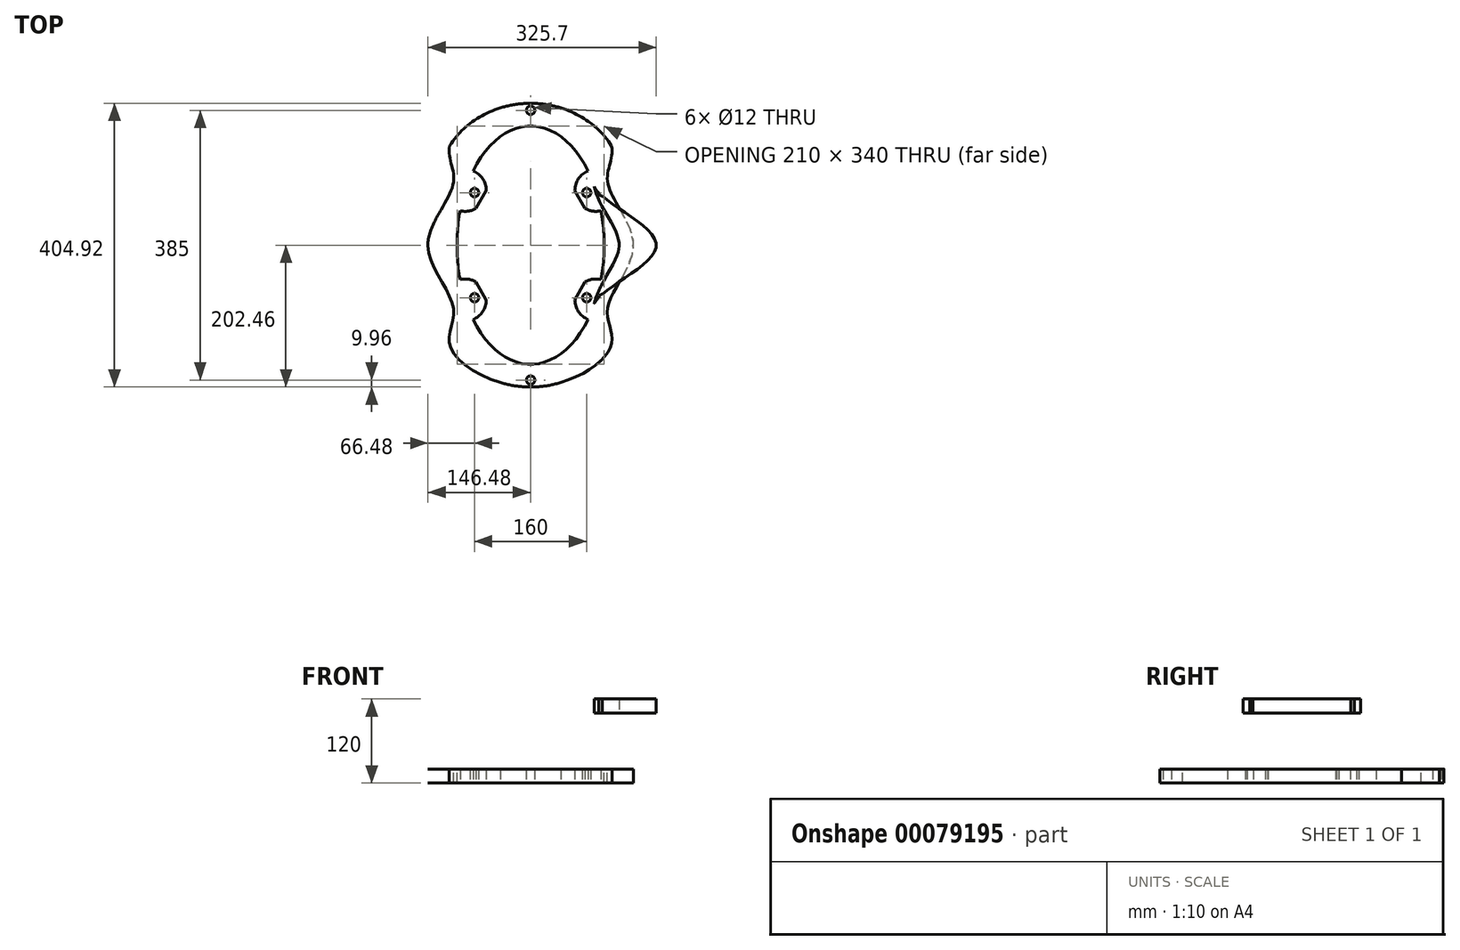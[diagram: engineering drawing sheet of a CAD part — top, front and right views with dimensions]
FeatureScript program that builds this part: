
annotation { "Feature Type Name" : "Feature", "Feature Type Description" : "" }
export const myFeature = defineFeature(function(context is Context, id is Id, definition is map)
    precondition{}
    {
        {
            var Q0;
            Q0=qCreatedBy(makeId("Top.planeOp"),FACE);
            var sketch = newSketch(context, id + "F0", { "sketchPlane" : qUnion([Q0])});
            skPoint(sketch, "E0", {"position": v(150.32, -165.76) * mm});
            skPoint(sketch, "E1", {"position": v(107.37, -221.56) * mm});
            skPoint(sketch, "E2", {"position": v(69.02, -211.72) * mm});
            skPoint(sketch, "E3", {"position": v(0, -246.18) * mm});
            skPoint(sketch, "E4", {"position": v(138.05, -177.25) * mm});
            skPoint(sketch, "E5", {"position": v(146.48, 0) * mm});
            skPoint(sketch, "E6", {"position": v(132.68, -82.88) * mm});
            skLineSegment(sketch, "E7", {"start": v(0, 292) * mm, "end": v(0, -246.18) * mm, "construction": true});
            skPoint(sketch, "E8.MirrorP", {"position": v(-146.48, 0) * mm});
            skPoint(sketch, "E9.MirrorP", {"position": v(-132.68, -82.88) * mm});
            skPoint(sketch, "E10.MirrorP", {"position": v(-150.32, -165.76) * mm});
            skPoint(sketch, "E11.MirrorP", {"position": v(-138.05, -177.25) * mm});
            skPoint(sketch, "E12.MirrorP", {"position": v(-107.37, -221.56) * mm});
            skPoint(sketch, "E13.MirrorP", {"position": v(-69.02, -211.72) * mm});
            skPoint(sketch, "E14", {"position": v(0, 0) * mm});
            skPoint(sketch, "E15", {"position": v(-146.25, -161.4) * mm});
            skPoint(sketch, "E16", {"position": v(-136.87, -189.28) * mm});
            skPoint(sketch, "E17", {"position": v(-146.26, -172.33) * mm});
            skPoint(sketch, "E18", {"position": v(-131.04, -210.06) * mm});
            skPoint(sketch, "E19", {"position": v(-94.82, -218.38) * mm});
            skPoint(sketch, "E20", {"position": v(-60.59, -222.84) * mm});
            skPoint(sketch, "E21", {"position": v(-67.25, -214.49) * mm});
            skPoint(sketch, "E22", {"position": v(-72.48, -210.2) * mm});
            skPoint(sketch, "E23", {"position": v(-119.37, -219.05) * mm});
            skPoint(sketch, "E24", {"position": v(-149.89, -167.68) * mm});
            skPoint(sketch, "E25.MirrorP", {"position": v(60.59, -222.84) * mm});
            skPoint(sketch, "E26.MirrorP", {"position": v(67.25, -214.49) * mm});
            skPoint(sketch, "E27.MirrorP", {"position": v(72.48, -210.2) * mm});
            skPoint(sketch, "E28.MirrorP", {"position": v(94.82, -218.38) * mm});
            skPoint(sketch, "E29.MirrorP", {"position": v(119.37, -219.05) * mm});
            skPoint(sketch, "E30.MirrorP", {"position": v(136.87, -189.28) * mm});
            skPoint(sketch, "E31.MirrorP", {"position": v(146.26, -172.33) * mm});
            skPoint(sketch, "E32.MirrorP", {"position": v(149.89, -167.68) * mm});
            skPoint(sketch, "E33.MirrorP", {"position": v(146.25, -161.4) * mm});
            skPoint(sketch, "E34", {"position": v(-139.73, -175.31) * mm});
            skPoint(sketch, "E35.MirrorP", {"position": v(131.04, -210.06) * mm});
            skPoint(sketch, "E36.MirrorP", {"position": v(-132.68, 82.88) * mm});
            skPoint(sketch, "E37.MirrorP", {"position": v(-139.73, 175.31) * mm});
            skPoint(sketch, "E38.MirrorP", {"position": v(-150.32, 165.76) * mm});
            skPoint(sketch, "E39.MirrorP", {"position": v(69.02, 211.72) * mm});
            skPoint(sketch, "E40.MirrorP", {"position": v(150.32, 165.76) * mm});
            skPoint(sketch, "E41.MirrorP", {"position": v(-67.25, 214.49) * mm});
            skPoint(sketch, "E42.MirrorP", {"position": v(131.04, 210.06) * mm});
            skPoint(sketch, "E43.MirrorP", {"position": v(60.59, 222.84) * mm});
            skPoint(sketch, "E44.MirrorP", {"position": v(119.37, 219.05) * mm});
            skPoint(sketch, "E45.MirrorP", {"position": v(136.87, 189.28) * mm});
            skPoint(sketch, "E46.MirrorP", {"position": v(-72.48, 210.2) * mm});
            skPoint(sketch, "E47.MirrorP", {"position": v(-138.05, 177.25) * mm});
            skPoint(sketch, "E48.MirrorP", {"position": v(-69.02, 211.72) * mm});
            skPoint(sketch, "E49.MirrorP", {"position": v(72.48, 210.2) * mm});
            skPoint(sketch, "E50.MirrorP", {"position": v(-146.25, 161.4) * mm});
            skPoint(sketch, "E51.MirrorP", {"position": v(-136.87, 189.28) * mm});
            skPoint(sketch, "E52.MirrorP", {"position": v(138.05, 177.25) * mm});
            skPoint(sketch, "E53.MirrorP", {"position": v(67.25, 214.49) * mm});
            skPoint(sketch, "E54.MirrorP", {"position": v(-149.89, 167.68) * mm});
            skPoint(sketch, "E55.MirrorP", {"position": v(149.89, 167.68) * mm});
            skPoint(sketch, "E56.MirrorP", {"position": v(-107.37, 221.56) * mm});
            skPoint(sketch, "E57.MirrorP", {"position": v(-94.82, 218.38) * mm});
            skPoint(sketch, "E58.MirrorP", {"position": v(146.26, 172.33) * mm});
            skPoint(sketch, "E59.MirrorP", {"position": v(107.37, 221.56) * mm});
            skPoint(sketch, "E60.MirrorP", {"position": v(-131.04, 210.06) * mm});
            skPoint(sketch, "E61.MirrorP", {"position": v(94.82, 218.38) * mm});
            skPoint(sketch, "E62.MirrorP", {"position": v(146.25, 161.4) * mm});
            skPoint(sketch, "E63.MirrorP", {"position": v(0, 246.18) * mm});
            skPoint(sketch, "E64.MirrorP", {"position": v(-146.26, 172.33) * mm});
            skPoint(sketch, "E65.MirrorP", {"position": v(-119.37, 219.05) * mm});
            skPoint(sketch, "E66.MirrorP", {"position": v(-60.59, 222.84) * mm});
            skPoint(sketch, "E67.MirrorP", {"position": v(132.68, 82.88) * mm});
            skFitSpline(sketch, "E68", {"points": [v(-146.48, 0) * mm, v(-132.68, 82.88) * mm, v(-146.25, 161.4) * mm, v(-150.32, 165.76) * mm, v(-149.89, 167.68) * mm, v(-146.26, 172.33) * mm, v(-139.73, 175.31) * mm, v(-138.05, 177.25) * mm, v(-136.87, 189.28) * mm, v(-131.04, 210.06) * mm, v(-119.37, 219.05) * mm, v(-107.37, 221.56) * mm, v(-94.82, 218.38) * mm, v(-72.48, 210.2) * mm, v(-69.02, 211.72) * mm, v(-67.25, 214.49) * mm, v(-60.59, 222.84) * mm, v(0, 246.18) * mm, v(60.59, 222.84) * mm, v(67.25, 214.49) * mm, v(69.02, 211.72) * mm, v(72.48, 210.2) * mm, v(94.82, 218.38) * mm, v(107.37, 221.56) * mm, v(119.37, 219.05) * mm, v(131.04, 210.06) * mm, v(136.87, 189.28) * mm, v(138.05, 177.25) * mm, v(146.26, 172.33) * mm, v(149.89, 167.68) * mm, v(150.32, 165.76) * mm, v(146.25, 161.4) * mm, v(132.68, 82.88) * mm, v(146.48, 0) * mm, v(132.68, -82.88) * mm, v(146.25, -161.4) * mm, v(150.32, -165.76) * mm, v(149.89, -167.68) * mm, v(146.26, -172.33) * mm, v(138.05, -177.25) * mm, v(136.87, -189.28) * mm, v(131.04, -210.06) * mm, v(119.37, -219.05) * mm, v(107.37, -221.56) * mm, v(94.82, -218.38) * mm, v(72.48, -210.2) * mm, v(69.02, -211.72) * mm, v(67.25, -214.49) * mm, v(60.59, -222.84) * mm, v(0, -246.18) * mm, v(-60.59, -222.84) * mm, v(-67.25, -214.49) * mm, v(-69.02, -211.72) * mm, v(-72.48, -210.2) * mm, v(-94.82, -218.38) * mm, v(-107.37, -221.56) * mm, v(-119.37, -219.05) * mm, v(-131.04, -210.06) * mm, v(-136.87, -189.28) * mm, v(-138.05, -177.25) * mm, v(-139.73, -175.31) * mm, v(-146.26, -172.33) * mm, v(-149.89, -167.68) * mm, v(-150.32, -165.76) * mm, v(-146.25, -161.4) * mm, v(-132.68, -82.88) * mm, v(-146.48, 0) * mm]});
            skPoint(sketch, "E69", {"position": v(0, 295) * mm});
            skPoint(sketch, "E70", {"position": v(-30, 295) * mm});
            skPoint(sketch, "E71", {"position": v(-225, 0) * mm});
            skPoint(sketch, "E72", {"position": v(-225, 100) * mm});
            skPoint(sketch, "E73.MirrorP", {"position": v(225, 100) * mm});
            skPoint(sketch, "E74.MirrorP", {"position": v(225, -60) * mm});
            skLineSegment(sketch, "E75", {"start": v(0, 0) * mm, "end": v(-373.3, 215.53) * mm, "construction": true});
            skLineSegment(sketch, "E76", {"start": v(0, 0) * mm, "end": v(-204.64, 354.44) * mm, "construction": true});
            skLineSegment(sketch, "E77", {"start": v(-225, 0) * mm, "end": v(-225, 100) * mm});
            skLineSegment(sketch, "E78", {"start": v(-30, 295) * mm, "end": v(0, 295) * mm});
            skPoint(sketch, "E79", {"position": v(-30, 100) * mm});
            skArc(sketch, "E80", {"start": v(-30, 295) * mm, "mid": v(-167.89, 237.89) * mm, "end": v(-225, 100) * mm});
            skLineSegment(sketch, "E81.MirrorCS", {"start": v(225, 0) * mm, "end": v(225, 100) * mm});
            skArc(sketch, "E82.MirrorCS", {"start": v(30, 295) * mm, "mid": v(167.89, 237.89) * mm, "end": v(225, 100) * mm});
            skLineSegment(sketch, "E83.MirrorCS", {"start": v(30, 295) * mm, "end": v(0, 295) * mm});
            skArc(sketch, "E84.MirrorCS", {"start": v(-30, -295) * mm, "mid": v(-167.89, -237.89) * mm, "end": v(-225, -100) * mm});
            skLineSegment(sketch, "E85.MirrorCS", {"start": v(-225, 0) * mm, "end": v(-225, -100) * mm});
            skLineSegment(sketch, "E86.MirrorCS", {"start": v(225, 0) * mm, "end": v(225, -100) * mm});
            skArc(sketch, "E87.MirrorCS", {"start": v(30, -295) * mm, "mid": v(167.89, -237.89) * mm, "end": v(225, -100) * mm});
            skLineSegment(sketch, "E88.MirrorCS", {"start": v(30, -295) * mm, "end": v(0, -295) * mm});
            skLineSegment(sketch, "E89.MirrorCS", {"start": v(-30, -295) * mm, "end": v(0, -295) * mm});
            skEllipse(sketch, "E90", {"center": v(0, 82.88) * mm, "majorRadius": 132.68 * mm, "minorRadius": 119.58 * mm, "majorAxis": v(1, 0)});
            skSolve(sketch);
        }
        {
            var Q0;
            {var subQ0=sQuery(id+"F0.wireOp",EDGE,"E90");var subQ1=sQuery(id+"F0.wireOp",EDGE,"E68");var subQ2=makeQuery(id+"F0.imprint","INTERSECT",VERTEX,{"disambiguationData":[OD(1.0)],"derivedFrom":[subQ1,subQ0]});Q0=makeQuery(id+"F0.imprint","IMPRINT",FACE,{"disambiguationData":[TD([[makeQuery(id+"F0.imprint","IMPRINT",EDGE,{"disambiguationData":[TD([[subQ2,1.0]])],"derivedFrom":subQ1}),-1.0]])]});}
            cPlane(context, id + "F1", {"entities" : qUnion([Q0]), "cplaneType" : CPlaneType.OFFSET, "offset" : 100 * mm, "width" : 150 * mm, "height" : 150 * mm});
        }
        {
            var Q0;
            {var subQ0=sQuery(id+"F0.wireOp",EDGE,"E90");var subQ1=sQuery(id+"F0.wireOp",EDGE,"E68");var subQ2=makeQuery(id+"F0.imprint","INTERSECT",VERTEX,{"disambiguationData":[OD(0.0)],"derivedFrom":[subQ1,subQ0]});Q0=makeQuery(id+"F0.imprint","IMPRINT",FACE,{"disambiguationData":[TD([[makeQuery(id+"F0.imprint","IMPRINT",EDGE,{"disambiguationData":[TD([[subQ2,1.0]])],"derivedFrom":subQ1}),-1.0]])]});}
            var sketch = newSketch(context, id + "F2", { "sketchPlane" : qUnion([Q0])});
            skFitSpline(sketch, "E91.0", {"points": [v(-146.48, 0) * mm, v(-146.48, 25.45) * mm, v(-122.55, 75.68) * mm, v(-141.58, 161.6) * mm, v(-150.97, 165.24) * mm, v(-149.84, 167.93) * mm, v(-146.88, 173.13) * mm, v(-139.54, 174.98) * mm, v(-137.39, 177.3) * mm, v(-137.38, 190.15) * mm, v(-133.28, 211.38) * mm, v(-119.9, 219.69) * mm, v(-106.83, 222.51) * mm, v(-95.46, 219.19) * mm, v(-72.9, 208.32) * mm, v(-68.89, 211.56) * mm, v(-66.98, 214.97) * mm, v(-60.9, 225.94) * mm, v(0, 260.58) * mm, v(60.9, 225.94) * mm, v(66.98, 214.97) * mm, v(68.89, 211.56) * mm, v(72.9, 208.32) * mm, v(95.47, 219.19) * mm, v(106.82, 222.52) * mm, v(119.95, 219.67) * mm, v(133.09, 211.44) * mm, v(138.2, 189.9) * mm, v(135.3, 175.97) * mm, v(146.9, 173.38) * mm, v(149.81, 167.94) * mm, v(150.98, 165.24) * mm, v(141.57, 161.6) * mm, v(122.55, 75.68) * mm, v(158.6, 0) * mm, v(122.55, -75.68) * mm, v(141.57, -161.6) * mm, v(150.98, -165.24) * mm, v(149.81, -167.94) * mm, v(146.9, -173.38) * mm, v(135.3, -175.97) * mm, v(138.2, -189.9) * mm, v(133.09, -211.44) * mm, v(119.95, -219.67) * mm, v(106.82, -222.52) * mm, v(95.47, -219.19) * mm, v(72.9, -208.32) * mm, v(68.89, -211.56) * mm, v(66.98, -214.97) * mm, v(60.9, -225.94) * mm, v(0, -260.58) * mm, v(-60.9, -225.94) * mm, v(-66.98, -214.97) * mm, v(-68.89, -211.56) * mm, v(-72.9, -208.32) * mm, v(-95.46, -219.19) * mm, v(-106.83, -222.51) * mm, v(-119.9, -219.69) * mm, v(-133.28, -211.38) * mm, v(-137.38, -190.15) * mm, v(-137.39, -177.3) * mm, v(-139.54, -174.98) * mm, v(-146.88, -173.13) * mm, v(-149.84, -167.93) * mm, v(-150.97, -165.24) * mm, v(-141.58, -161.6) * mm, v(-122.55, -75.68) * mm, v(-146.48, -25.45) * mm, v(-146.48, 0) * mm]});
            skEllipticalArc(sketch, "E92.0", {});
            skEllipticalArc(sketch, "E93.MirrorC", {});
            skFitSpline(sketch, "E94.trimOffspring", {"points": [v(-146.48, 0) * mm, v(-146.48, 25.45) * mm, v(-122.55, 75.68) * mm, v(-141.58, 161.6) * mm, v(-150.97, 165.24) * mm, v(-149.84, 167.93) * mm, v(-146.88, 173.13) * mm, v(-139.54, 174.98) * mm, v(-137.39, 177.3) * mm, v(-137.38, 190.15) * mm, v(-133.28, 211.38) * mm, v(-119.9, 219.69) * mm, v(-106.83, 222.51) * mm, v(-95.46, 219.19) * mm, v(-72.9, 208.32) * mm, v(-68.89, 211.56) * mm, v(-66.98, 214.97) * mm, v(-60.9, 225.94) * mm, v(0, 260.58) * mm, v(60.9, 225.94) * mm, v(66.98, 214.97) * mm, v(68.89, 211.56) * mm, v(72.9, 208.32) * mm, v(95.47, 219.19) * mm, v(106.82, 222.52) * mm, v(119.95, 219.67) * mm, v(133.09, 211.44) * mm, v(138.2, 189.9) * mm, v(135.3, 175.97) * mm, v(146.9, 173.38) * mm, v(149.81, 167.94) * mm, v(150.98, 165.24) * mm, v(141.57, 161.6) * mm, v(122.55, 75.68) * mm, v(158.6, 0) * mm, v(122.55, -75.68) * mm, v(141.57, -161.6) * mm, v(150.98, -165.24) * mm, v(149.81, -167.94) * mm, v(146.9, -173.38) * mm, v(135.3, -175.97) * mm, v(138.2, -189.9) * mm, v(133.09, -211.44) * mm, v(119.95, -219.67) * mm, v(106.82, -222.52) * mm, v(95.47, -219.19) * mm, v(72.9, -208.32) * mm, v(68.89, -211.56) * mm, v(66.98, -214.97) * mm, v(60.9, -225.94) * mm, v(0, -260.58) * mm, v(-60.9, -225.94) * mm, v(-66.98, -214.97) * mm, v(-68.89, -211.56) * mm, v(-72.9, -208.32) * mm, v(-95.46, -219.19) * mm, v(-106.83, -222.51) * mm, v(-119.9, -219.69) * mm, v(-133.28, -211.38) * mm, v(-137.38, -190.15) * mm, v(-137.39, -177.3) * mm, v(-139.54, -174.98) * mm, v(-146.88, -173.13) * mm, v(-149.84, -167.93) * mm, v(-150.97, -165.24) * mm, v(-141.58, -161.6) * mm, v(-122.55, -75.68) * mm, v(-146.48, -25.45) * mm, v(-146.48, 0) * mm]});
            skPoint(sketch, "E95", {"position": v(0, 202.46) * mm});
            skPoint(sketch, "E96", {"position": v(-110, 90) * mm});
            skPoint(sketch, "E97", {"position": v(-115, 143) * mm});
            skPoint(sketch, "E98.MirrorP", {"position": v(115, 143) * mm});
            skPoint(sketch, "E99.MirrorP", {"position": v(110, 90) * mm});
            skPoint(sketch, "E100.MirrorP", {"position": v(-110, -90) * mm});
            skPoint(sketch, "E101.MirrorP", {"position": v(-115, -143) * mm});
            skPoint(sketch, "E102.MirrorP", {"position": v(0, -202.46) * mm});
            skPoint(sketch, "E103.MirrorP", {"position": v(115, -143) * mm});
            skPoint(sketch, "E104.MirrorP", {"position": v(110, -90) * mm});
            skFitSpline(sketch, "E105", {"points": [v(-146.48, 0) * mm, v(-110, 90) * mm, v(-115, 143) * mm, v(0, 202.46) * mm, v(115, 143) * mm, v(110, 90) * mm, v(146.48, 0) * mm, v(110, -90) * mm, v(115, -143) * mm, v(0, -202.46) * mm, v(-115, -143) * mm, v(-110, -90) * mm, v(-146.48, 0) * mm]});
            skFitSpline(sketch, "E106.trimOffspring", {"points": [v(-146.48, 0) * mm, v(-146.48, 25.45) * mm, v(-122.55, 75.68) * mm, v(-141.58, 161.6) * mm, v(-150.97, 165.24) * mm, v(-149.84, 167.93) * mm, v(-146.88, 173.13) * mm, v(-139.54, 174.98) * mm, v(-137.39, 177.3) * mm, v(-137.38, 190.15) * mm, v(-133.28, 211.38) * mm, v(-119.9, 219.69) * mm, v(-106.83, 222.51) * mm, v(-95.46, 219.19) * mm, v(-72.9, 208.32) * mm, v(-68.89, 211.56) * mm, v(-66.98, 214.97) * mm, v(-60.9, 225.94) * mm, v(0, 260.58) * mm, v(60.9, 225.94) * mm, v(66.98, 214.97) * mm, v(68.89, 211.56) * mm, v(72.9, 208.32) * mm, v(95.47, 219.19) * mm, v(106.82, 222.52) * mm, v(119.95, 219.67) * mm, v(133.09, 211.44) * mm, v(138.2, 189.9) * mm, v(135.3, 175.97) * mm, v(146.9, 173.38) * mm, v(149.81, 167.94) * mm, v(150.98, 165.24) * mm, v(141.57, 161.6) * mm, v(122.55, 75.68) * mm, v(158.6, 0) * mm, v(122.55, -75.68) * mm, v(141.57, -161.6) * mm, v(150.98, -165.24) * mm, v(149.81, -167.94) * mm, v(146.9, -173.38) * mm, v(135.3, -175.97) * mm, v(138.2, -189.9) * mm, v(133.09, -211.44) * mm, v(119.95, -219.67) * mm, v(106.82, -222.52) * mm, v(95.47, -219.19) * mm, v(72.9, -208.32) * mm, v(68.89, -211.56) * mm, v(66.98, -214.97) * mm, v(60.9, -225.94) * mm, v(0, -260.58) * mm, v(-60.9, -225.94) * mm, v(-66.98, -214.97) * mm, v(-68.89, -211.56) * mm, v(-72.9, -208.32) * mm, v(-95.46, -219.19) * mm, v(-106.83, -222.51) * mm, v(-119.9, -219.69) * mm, v(-133.28, -211.38) * mm, v(-137.38, -190.15) * mm, v(-137.39, -177.3) * mm, v(-139.54, -174.98) * mm, v(-146.88, -173.13) * mm, v(-149.84, -167.93) * mm, v(-150.97, -165.24) * mm, v(-141.58, -161.6) * mm, v(-122.55, -75.68) * mm, v(-146.48, -25.45) * mm, v(-146.48, 0) * mm]});
            skFitSpline(sketch, "E107.trimOffspring", {"points": [v(-146.48, 0) * mm, v(-146.48, 25.45) * mm, v(-122.55, 75.68) * mm, v(-141.58, 161.6) * mm, v(-150.97, 165.24) * mm, v(-149.84, 167.93) * mm, v(-146.88, 173.13) * mm, v(-139.54, 174.98) * mm, v(-137.39, 177.3) * mm, v(-137.38, 190.15) * mm, v(-133.28, 211.38) * mm, v(-119.9, 219.69) * mm, v(-106.83, 222.51) * mm, v(-95.46, 219.19) * mm, v(-72.9, 208.32) * mm, v(-68.89, 211.56) * mm, v(-66.98, 214.97) * mm, v(-60.9, 225.94) * mm, v(0, 260.58) * mm, v(60.9, 225.94) * mm, v(66.98, 214.97) * mm, v(68.89, 211.56) * mm, v(72.9, 208.32) * mm, v(95.47, 219.19) * mm, v(106.82, 222.52) * mm, v(119.95, 219.67) * mm, v(133.09, 211.44) * mm, v(138.2, 189.9) * mm, v(135.3, 175.97) * mm, v(146.9, 173.38) * mm, v(149.81, 167.94) * mm, v(150.98, 165.24) * mm, v(141.57, 161.6) * mm, v(122.55, 75.68) * mm, v(158.6, 0) * mm, v(122.55, -75.68) * mm, v(141.57, -161.6) * mm, v(150.98, -165.24) * mm, v(149.81, -167.94) * mm, v(146.9, -173.38) * mm, v(135.3, -175.97) * mm, v(138.2, -189.9) * mm, v(133.09, -211.44) * mm, v(119.95, -219.67) * mm, v(106.82, -222.52) * mm, v(95.47, -219.19) * mm, v(72.9, -208.32) * mm, v(68.89, -211.56) * mm, v(66.98, -214.97) * mm, v(60.9, -225.94) * mm, v(0, -260.58) * mm, v(-60.9, -225.94) * mm, v(-66.98, -214.97) * mm, v(-68.89, -211.56) * mm, v(-72.9, -208.32) * mm, v(-95.46, -219.19) * mm, v(-106.83, -222.51) * mm, v(-119.9, -219.69) * mm, v(-133.28, -211.38) * mm, v(-137.38, -190.15) * mm, v(-137.39, -177.3) * mm, v(-139.54, -174.98) * mm, v(-146.88, -173.13) * mm, v(-149.84, -167.93) * mm, v(-150.97, -165.24) * mm, v(-141.58, -161.6) * mm, v(-122.55, -75.68) * mm, v(-146.48, -25.45) * mm, v(-146.48, 0) * mm]});
            skFitSpline(sketch, "E108.trimOffspring", {"points": [v(-146.48, 0) * mm, v(-146.48, 25.45) * mm, v(-122.55, 75.68) * mm, v(-141.58, 161.6) * mm, v(-150.97, 165.24) * mm, v(-149.84, 167.93) * mm, v(-146.88, 173.13) * mm, v(-139.54, 174.98) * mm, v(-137.39, 177.3) * mm, v(-137.38, 190.15) * mm, v(-133.28, 211.38) * mm, v(-119.9, 219.69) * mm, v(-106.83, 222.51) * mm, v(-95.46, 219.19) * mm, v(-72.9, 208.32) * mm, v(-68.89, 211.56) * mm, v(-66.98, 214.97) * mm, v(-60.9, 225.94) * mm, v(0, 260.58) * mm, v(60.9, 225.94) * mm, v(66.98, 214.97) * mm, v(68.89, 211.56) * mm, v(72.9, 208.32) * mm, v(95.47, 219.19) * mm, v(106.82, 222.52) * mm, v(119.95, 219.67) * mm, v(133.09, 211.44) * mm, v(138.2, 189.9) * mm, v(135.3, 175.97) * mm, v(146.9, 173.38) * mm, v(149.81, 167.94) * mm, v(150.98, 165.24) * mm, v(141.57, 161.6) * mm, v(122.55, 75.68) * mm, v(158.6, 0) * mm, v(122.55, -75.68) * mm, v(141.57, -161.6) * mm, v(150.98, -165.24) * mm, v(149.81, -167.94) * mm, v(146.9, -173.38) * mm, v(135.3, -175.97) * mm, v(138.2, -189.9) * mm, v(133.09, -211.44) * mm, v(119.95, -219.67) * mm, v(106.82, -222.52) * mm, v(95.47, -219.19) * mm, v(72.9, -208.32) * mm, v(68.89, -211.56) * mm, v(66.98, -214.97) * mm, v(60.9, -225.94) * mm, v(0, -260.58) * mm, v(-60.9, -225.94) * mm, v(-66.98, -214.97) * mm, v(-68.89, -211.56) * mm, v(-72.9, -208.32) * mm, v(-95.46, -219.19) * mm, v(-106.83, -222.51) * mm, v(-119.9, -219.69) * mm, v(-133.28, -211.38) * mm, v(-137.38, -190.15) * mm, v(-137.39, -177.3) * mm, v(-139.54, -174.98) * mm, v(-146.88, -173.13) * mm, v(-149.84, -167.93) * mm, v(-150.97, -165.24) * mm, v(-141.58, -161.6) * mm, v(-122.55, -75.68) * mm, v(-146.48, -25.45) * mm, v(-146.48, 0) * mm]});
            skEllipticalArc(sketch, "E109.trimOffspring", {});
            skEllipticalArc(sketch, "E110.trimOffspring", {});
            skEllipticalArc(sketch, "E111.trimOffspring", {});
            skEllipticalArc(sketch, "E112.trimOffspring", {});
            skCircle(sketch, "E113", {"center": v(0, 192.5) * mm, "radius": 6 * mm});
            skLineSegment(sketch, "E114", {"start": v(-226.31, 0) * mm, "end": v(229.86, 0) * mm, "construction": true});
            skCircle(sketch, "E115.MirrorC", {"center": v(0, -192.5) * mm, "radius": 6 * mm});
            skPoint(sketch, "E116", {"position": v(-80, 75) * mm});
            skCircle(sketch, "E117", {"center": v(-80, 75) * mm, "radius": 6 * mm});
            skArc(sketch, "E118", {"start": v(-100.52, 49.11) * mm, "mid": v(-88.85, 48.53) * mm, "end": v(-77.84, 52.46) * mm});
            skFitSpline(sketch, "E119.0", {"points": [v(-126.48, -0.62) * mm, v(-126.48, 0) * mm, v(-126.48, 0.62) * mm, v(-126.45, 1.48) * mm, v(-126.37, 2.57) * mm, v(-126.23, 3.92) * mm, v(-125.95, 5.8) * mm, v(-125.44, 8.25) * mm, v(-124.57, 11.4) * mm, v(-123.44, 14.7) * mm, v(-121.62, 19.33) * mm, v(-118.77, 25.43) * mm, v(-114.67, 33.14) * mm, v(-110.1, 41.14) * mm, v(-105.34, 49.38) * mm, v(-101.43, 56.47) * mm, v(-98.47, 62.31) * mm, v(-96.37, 66.81) * mm, v(-94.44, 71.44) * mm, v(-93, 75.45) * mm, v(-92, 78.76) * mm, v(-91.33, 81.3) * mm, v(-90.75, 83.9) * mm, v(-90.35, 86.12) * mm, v(-90.1, 87.93) * mm, v(-89.88, 89.73) * mm, v(-89.7, 91.94) * mm, v(-89.6, 94.53) * mm, v(-89.61, 97.06) * mm, v(-89.72, 99.51) * mm, v(-89.98, 102.68) * mm, v(-90.47, 106.44) * mm, v(-91.26, 110.63) * mm, v(-92.14, 114.5) * mm, v(-93.04, 118.06) * mm, v(-94.2, 122.4) * mm, v(-95.17, 126.15) * mm, v(-95.82, 129.29) * mm, v(-96.14, 131.32) * mm, v(-96.3, 133.04) * mm, v(-96.31, 134.46) * mm, v(-96.23, 135.45) * mm, v(-96.11, 136.18) * mm, v(-96.02, 136.62) * mm, v(-95.93, 136.97) * mm, v(-95.85, 137.24) * mm, v(-95.76, 137.52) * mm, v(-95.62, 137.93) * mm, v(-95.4, 138.5) * mm, v(-94.93, 139.51) * mm, v(-94.14, 140.98) * mm, v(-92.83, 143) * mm, v(-91.14, 145.21) * mm, v(-89.1, 147.56) * mm, v(-86.7, 150.02) * mm, v(-83.04, 153.37) * mm, v(-77.67, 157.62) * mm, v(-70.12, 162.62) * mm, v(-61.63, 167.33) * mm, v(-52.35, 171.62) * mm, v(-42.46, 175.35) * mm, v(-32.12, 178.4) * mm, v(-23.26, 180.32) * mm, v(-16.1, 181.41) * mm, v(-10.72, 182.01) * mm, v(-6.24, 182.32) * mm, v(-2.67, 182.44) * mm, v(0, 182.47) * mm, v(2.67, 182.44) * mm, v(6.24, 182.32) * mm, v(10.72, 182.01) * mm, v(16.1, 181.41) * mm, v(23.26, 180.32) * mm, v(32.12, 178.4) * mm, v(42.46, 175.35) * mm, v(52.35, 171.62) * mm, v(61.63, 167.33) * mm, v(70.12, 162.62) * mm, v(77.67, 157.62) * mm, v(83.04, 153.37) * mm, v(86.7, 150.02) * mm, v(89.1, 147.56) * mm, v(91.14, 145.21) * mm, v(92.83, 143) * mm, v(94.14, 140.98) * mm, v(94.93, 139.51) * mm, v(95.4, 138.5) * mm, v(95.62, 137.93) * mm, v(95.76, 137.52) * mm, v(95.85, 137.24) * mm, v(95.93, 136.97) * mm, v(96.02, 136.62) * mm, v(96.11, 136.18) * mm, v(96.23, 135.45) * mm, v(96.31, 134.46) * mm, v(96.3, 133.04) * mm, v(96.14, 131.32) * mm, v(95.82, 129.29) * mm, v(95.17, 126.15) * mm, v(94.2, 122.4) * mm, v(93.04, 118.06) * mm, v(92.14, 114.5) * mm, v(91.26, 110.63) * mm, v(90.47, 106.44) * mm, v(89.98, 102.68) * mm, v(89.72, 99.51) * mm, v(89.61, 97.06) * mm, v(89.6, 94.53) * mm, v(89.7, 91.94) * mm, v(89.88, 89.73) * mm, v(90.1, 87.93) * mm, v(90.35, 86.12) * mm, v(90.75, 83.9) * mm, v(91.33, 81.3) * mm, v(92, 78.76) * mm, v(93, 75.45) * mm, v(94.44, 71.44) * mm, v(96.37, 66.81) * mm, v(98.47, 62.31) * mm, v(101.43, 56.47) * mm, v(105.34, 49.38) * mm, v(110.1, 41.14) * mm, v(114.67, 33.14) * mm, v(118.77, 25.43) * mm, v(121.62, 19.33) * mm, v(123.44, 14.7) * mm, v(124.57, 11.4) * mm, v(125.44, 8.25) * mm, v(125.95, 5.8) * mm, v(126.23, 3.92) * mm, v(126.37, 2.57) * mm, v(126.45, 1.48) * mm, v(126.48, 0.62) * mm, v(126.48, 0) * mm, v(126.48, -0.62) * mm, v(126.45, -1.48) * mm, v(126.37, -2.57) * mm, v(126.23, -3.92) * mm, v(125.95, -5.8) * mm, v(125.44, -8.25) * mm, v(124.57, -11.4) * mm, v(123.44, -14.7) * mm, v(121.62, -19.33) * mm, v(118.77, -25.43) * mm, v(114.67, -33.14) * mm, v(110.1, -41.14) * mm, v(105.34, -49.38) * mm, v(101.43, -56.47) * mm, v(98.47, -62.31) * mm, v(96.37, -66.81) * mm, v(94.44, -71.44) * mm, v(93, -75.45) * mm, v(92, -78.76) * mm, v(91.33, -81.3) * mm, v(90.75, -83.9) * mm, v(90.35, -86.12) * mm, v(90.1, -87.93) * mm, v(89.88, -89.73) * mm, v(89.7, -91.94) * mm, v(89.6, -94.53) * mm, v(89.61, -97.06) * mm, v(89.72, -99.51) * mm, v(89.98, -102.68) * mm, v(90.47, -106.44) * mm, v(91.26, -110.63) * mm, v(92.14, -114.5) * mm, v(93.04, -118.06) * mm, v(94.2, -122.4) * mm, v(95.17, -126.15) * mm, v(95.82, -129.29) * mm, v(96.14, -131.32) * mm, v(96.3, -133.04) * mm, v(96.31, -134.46) * mm, v(96.23, -135.45) * mm, v(96.11, -136.18) * mm, v(96.02, -136.62) * mm, v(95.93, -136.97) * mm, v(95.85, -137.24) * mm, v(95.76, -137.52) * mm, v(95.62, -137.93) * mm, v(95.4, -138.5) * mm, v(94.93, -139.51) * mm, v(94.14, -140.98) * mm, v(92.83, -143) * mm, v(91.14, -145.21) * mm, v(89.1, -147.56) * mm, v(86.7, -150.02) * mm, v(83.04, -153.37) * mm, v(77.67, -157.62) * mm, v(70.12, -162.62) * mm, v(61.63, -167.33) * mm, v(52.35, -171.62) * mm, v(42.46, -175.35) * mm, v(32.12, -178.4) * mm, v(23.26, -180.32) * mm, v(16.1, -181.41) * mm, v(10.72, -182.01) * mm, v(6.24, -182.32) * mm, v(2.67, -182.44) * mm, v(0, -182.47) * mm, v(-2.67, -182.44) * mm, v(-6.24, -182.32) * mm, v(-10.72, -182.01) * mm, v(-16.1, -181.41) * mm, v(-23.26, -180.32) * mm, v(-32.12, -178.4) * mm, v(-42.46, -175.35) * mm, v(-52.35, -171.62) * mm, v(-61.63, -167.33) * mm, v(-70.12, -162.62) * mm, v(-77.67, -157.62) * mm, v(-83.04, -153.37) * mm, v(-86.7, -150.02) * mm, v(-89.1, -147.56) * mm, v(-91.14, -145.21) * mm, v(-92.83, -143) * mm, v(-94.14, -140.98) * mm, v(-94.93, -139.51) * mm, v(-95.4, -138.5) * mm, v(-95.62, -137.93) * mm, v(-95.76, -137.52) * mm, v(-95.85, -137.24) * mm, v(-95.93, -136.97) * mm, v(-96.02, -136.62) * mm, v(-96.11, -136.18) * mm, v(-96.23, -135.45) * mm, v(-96.31, -134.46) * mm, v(-96.3, -133.04) * mm, v(-96.14, -131.32) * mm, v(-95.82, -129.29) * mm, v(-95.17, -126.15) * mm, v(-94.2, -122.4) * mm, v(-93.04, -118.06) * mm, v(-92.14, -114.5) * mm, v(-91.26, -110.63) * mm, v(-90.47, -106.44) * mm, v(-89.98, -102.68) * mm, v(-89.72, -99.51) * mm, v(-89.61, -97.06) * mm, v(-89.6, -94.53) * mm, v(-89.7, -91.94) * mm, v(-89.88, -89.73) * mm, v(-90.1, -87.93) * mm, v(-90.35, -86.12) * mm, v(-90.75, -83.9) * mm, v(-91.33, -81.3) * mm, v(-92, -78.76) * mm, v(-93, -75.45) * mm, v(-94.44, -71.44) * mm, v(-96.37, -66.81) * mm, v(-98.47, -62.31) * mm, v(-101.43, -56.47) * mm, v(-105.34, -49.38) * mm, v(-110.1, -41.14) * mm, v(-114.67, -33.14) * mm, v(-118.77, -25.43) * mm, v(-121.62, -19.33) * mm, v(-123.44, -14.7) * mm, v(-124.57, -11.4) * mm, v(-125.44, -8.25) * mm, v(-125.95, -5.8) * mm, v(-126.23, -3.92) * mm, v(-126.37, -2.57) * mm, v(-126.45, -1.48) * mm, v(-126.48, -0.62) * mm, v(-126.48, 0) * mm, v(-126.48, 0.62) * mm]});
            skArc(sketch, "E120.MirrorCS", {"start": v(-100.52, -49.11) * mm, "mid": v(-88.85, -48.53) * mm, "end": v(-77.84, -52.46) * mm});
            skCircle(sketch, "E121.MirrorC", {"center": v(-80, -75) * mm, "radius": 6 * mm});
            skArc(sketch, "E122.MirrorCS", {"start": v(100.52, -49.11) * mm, "mid": v(88.85, -48.53) * mm, "end": v(77.84, -52.46) * mm});
            skCircle(sketch, "E123.MirrorC", {"center": v(80, -75) * mm, "radius": 6 * mm});
            skArc(sketch, "E124.MirrorCS", {"start": v(100.52, 49.11) * mm, "mid": v(88.85, 48.53) * mm, "end": v(77.84, 52.46) * mm});
            skCircle(sketch, "E125.MirrorC", {"center": v(80, 75) * mm, "radius": 6 * mm});
            skEllipticalArc(sketch, "E126.trimOffspring", {});
            skEllipticalArc(sketch, "E127.trimOffspring", {});
            skEllipticalArc(sketch, "E128.trimOffspring", {});
            skEllipticalArc(sketch, "E129.trimOffspring", {});
            skFitSpline(sketch, "E130.trimOffspring", {"points": [v(-126.48, -0.62) * mm, v(-126.48, 0) * mm, v(-126.48, 0.62) * mm, v(-126.45, 1.48) * mm, v(-126.37, 2.57) * mm, v(-126.23, 3.92) * mm, v(-125.95, 5.8) * mm, v(-125.44, 8.25) * mm, v(-124.57, 11.4) * mm, v(-123.44, 14.7) * mm, v(-121.62, 19.33) * mm, v(-118.77, 25.43) * mm, v(-114.67, 33.14) * mm, v(-110.1, 41.14) * mm, v(-105.34, 49.38) * mm, v(-101.43, 56.47) * mm, v(-98.47, 62.31) * mm, v(-96.37, 66.81) * mm, v(-94.44, 71.44) * mm, v(-93, 75.45) * mm, v(-92, 78.76) * mm, v(-91.33, 81.3) * mm, v(-90.75, 83.9) * mm, v(-90.35, 86.12) * mm, v(-90.1, 87.93) * mm, v(-89.88, 89.73) * mm, v(-89.7, 91.94) * mm, v(-89.6, 94.53) * mm, v(-89.61, 97.06) * mm, v(-89.72, 99.51) * mm, v(-89.98, 102.68) * mm, v(-90.47, 106.44) * mm, v(-91.26, 110.63) * mm, v(-92.14, 114.5) * mm, v(-93.04, 118.06) * mm, v(-94.2, 122.4) * mm, v(-95.17, 126.15) * mm, v(-95.82, 129.29) * mm, v(-96.14, 131.32) * mm, v(-96.3, 133.04) * mm, v(-96.31, 134.46) * mm, v(-96.23, 135.45) * mm, v(-96.11, 136.18) * mm, v(-96.02, 136.62) * mm, v(-95.93, 136.97) * mm, v(-95.85, 137.24) * mm, v(-95.76, 137.52) * mm, v(-95.62, 137.93) * mm, v(-95.4, 138.5) * mm, v(-94.93, 139.51) * mm, v(-94.14, 140.98) * mm, v(-92.83, 143) * mm, v(-91.14, 145.21) * mm, v(-89.1, 147.56) * mm, v(-86.7, 150.02) * mm, v(-83.04, 153.37) * mm, v(-77.67, 157.62) * mm, v(-70.12, 162.62) * mm, v(-61.63, 167.33) * mm, v(-52.35, 171.62) * mm, v(-42.46, 175.35) * mm, v(-32.12, 178.4) * mm, v(-23.26, 180.32) * mm, v(-16.1, 181.41) * mm, v(-10.72, 182.01) * mm, v(-6.24, 182.32) * mm, v(-2.67, 182.44) * mm, v(0, 182.47) * mm, v(2.67, 182.44) * mm, v(6.24, 182.32) * mm, v(10.72, 182.01) * mm, v(16.1, 181.41) * mm, v(23.26, 180.32) * mm, v(32.12, 178.4) * mm, v(42.46, 175.35) * mm, v(52.35, 171.62) * mm, v(61.63, 167.33) * mm, v(70.12, 162.62) * mm, v(77.67, 157.62) * mm, v(83.04, 153.37) * mm, v(86.7, 150.02) * mm, v(89.1, 147.56) * mm, v(91.14, 145.21) * mm, v(92.83, 143) * mm, v(94.14, 140.98) * mm, v(94.93, 139.51) * mm, v(95.4, 138.5) * mm, v(95.62, 137.93) * mm, v(95.76, 137.52) * mm, v(95.85, 137.24) * mm, v(95.93, 136.97) * mm, v(96.02, 136.62) * mm, v(96.11, 136.18) * mm, v(96.23, 135.45) * mm, v(96.31, 134.46) * mm, v(96.3, 133.04) * mm, v(96.14, 131.32) * mm, v(95.82, 129.29) * mm, v(95.17, 126.15) * mm, v(94.2, 122.4) * mm, v(93.04, 118.06) * mm, v(92.14, 114.5) * mm, v(91.26, 110.63) * mm, v(90.47, 106.44) * mm, v(89.98, 102.68) * mm, v(89.72, 99.51) * mm, v(89.61, 97.06) * mm, v(89.6, 94.53) * mm, v(89.7, 91.94) * mm, v(89.88, 89.73) * mm, v(90.1, 87.93) * mm, v(90.35, 86.12) * mm, v(90.75, 83.9) * mm, v(91.33, 81.3) * mm, v(92, 78.76) * mm, v(93, 75.45) * mm, v(94.44, 71.44) * mm, v(96.37, 66.81) * mm, v(98.47, 62.31) * mm, v(101.43, 56.47) * mm, v(105.34, 49.38) * mm, v(110.1, 41.14) * mm, v(114.67, 33.14) * mm, v(118.77, 25.43) * mm, v(121.62, 19.33) * mm, v(123.44, 14.7) * mm, v(124.57, 11.4) * mm, v(125.44, 8.25) * mm, v(125.95, 5.8) * mm, v(126.23, 3.92) * mm, v(126.37, 2.57) * mm, v(126.45, 1.48) * mm, v(126.48, 0.62) * mm, v(126.48, 0) * mm, v(126.48, -0.62) * mm, v(126.45, -1.48) * mm, v(126.37, -2.57) * mm, v(126.23, -3.92) * mm, v(125.95, -5.8) * mm, v(125.44, -8.25) * mm, v(124.57, -11.4) * mm, v(123.44, -14.7) * mm, v(121.62, -19.33) * mm, v(118.77, -25.43) * mm, v(114.67, -33.14) * mm, v(110.1, -41.14) * mm, v(105.34, -49.38) * mm, v(101.43, -56.47) * mm, v(98.47, -62.31) * mm, v(96.37, -66.81) * mm, v(94.44, -71.44) * mm, v(93, -75.45) * mm, v(92, -78.76) * mm, v(91.33, -81.3) * mm, v(90.75, -83.9) * mm, v(90.35, -86.12) * mm, v(90.1, -87.93) * mm, v(89.88, -89.73) * mm, v(89.7, -91.94) * mm, v(89.6, -94.53) * mm, v(89.61, -97.06) * mm, v(89.72, -99.51) * mm, v(89.98, -102.68) * mm, v(90.47, -106.44) * mm, v(91.26, -110.63) * mm, v(92.14, -114.5) * mm, v(93.04, -118.06) * mm, v(94.2, -122.4) * mm, v(95.17, -126.15) * mm, v(95.82, -129.29) * mm, v(96.14, -131.32) * mm, v(96.3, -133.04) * mm, v(96.31, -134.46) * mm, v(96.23, -135.45) * mm, v(96.11, -136.18) * mm, v(96.02, -136.62) * mm, v(95.93, -136.97) * mm, v(95.85, -137.24) * mm, v(95.76, -137.52) * mm, v(95.62, -137.93) * mm, v(95.4, -138.5) * mm, v(94.93, -139.51) * mm, v(94.14, -140.98) * mm, v(92.83, -143) * mm, v(91.14, -145.21) * mm, v(89.1, -147.56) * mm, v(86.7, -150.02) * mm, v(83.04, -153.37) * mm, v(77.67, -157.62) * mm, v(70.12, -162.62) * mm, v(61.63, -167.33) * mm, v(52.35, -171.62) * mm, v(42.46, -175.35) * mm, v(32.12, -178.4) * mm, v(23.26, -180.32) * mm, v(16.1, -181.41) * mm, v(10.72, -182.01) * mm, v(6.24, -182.32) * mm, v(2.67, -182.44) * mm, v(0, -182.47) * mm, v(-2.67, -182.44) * mm, v(-6.24, -182.32) * mm, v(-10.72, -182.01) * mm, v(-16.1, -181.41) * mm, v(-23.26, -180.32) * mm, v(-32.12, -178.4) * mm, v(-42.46, -175.35) * mm, v(-52.35, -171.62) * mm, v(-61.63, -167.33) * mm, v(-70.12, -162.62) * mm, v(-77.67, -157.62) * mm, v(-83.04, -153.37) * mm, v(-86.7, -150.02) * mm, v(-89.1, -147.56) * mm, v(-91.14, -145.21) * mm, v(-92.83, -143) * mm, v(-94.14, -140.98) * mm, v(-94.93, -139.51) * mm, v(-95.4, -138.5) * mm, v(-95.62, -137.93) * mm, v(-95.76, -137.52) * mm, v(-95.85, -137.24) * mm, v(-95.93, -136.97) * mm, v(-96.02, -136.62) * mm, v(-96.11, -136.18) * mm, v(-96.23, -135.45) * mm, v(-96.31, -134.46) * mm, v(-96.3, -133.04) * mm, v(-96.14, -131.32) * mm, v(-95.82, -129.29) * mm, v(-95.17, -126.15) * mm, v(-94.2, -122.4) * mm, v(-93.04, -118.06) * mm, v(-92.14, -114.5) * mm, v(-91.26, -110.63) * mm, v(-90.47, -106.44) * mm, v(-89.98, -102.68) * mm, v(-89.72, -99.51) * mm, v(-89.61, -97.06) * mm, v(-89.6, -94.53) * mm, v(-89.7, -91.94) * mm, v(-89.88, -89.73) * mm, v(-90.1, -87.93) * mm, v(-90.35, -86.12) * mm, v(-90.75, -83.9) * mm, v(-91.33, -81.3) * mm, v(-92, -78.76) * mm, v(-93, -75.45) * mm, v(-94.44, -71.44) * mm, v(-96.37, -66.81) * mm, v(-98.47, -62.31) * mm, v(-101.43, -56.47) * mm, v(-105.34, -49.38) * mm, v(-110.1, -41.14) * mm, v(-114.67, -33.14) * mm, v(-118.77, -25.43) * mm, v(-121.62, -19.33) * mm, v(-123.44, -14.7) * mm, v(-124.57, -11.4) * mm, v(-125.44, -8.25) * mm, v(-125.95, -5.8) * mm, v(-126.23, -3.92) * mm, v(-126.37, -2.57) * mm, v(-126.45, -1.48) * mm, v(-126.48, -0.62) * mm, v(-126.48, 0) * mm, v(-126.48, 0.62) * mm]});
            skFitSpline(sketch, "E131.trimOffspring", {"points": [v(-126.48, -0.62) * mm, v(-126.48, 0) * mm, v(-126.48, 0.62) * mm, v(-126.45, 1.48) * mm, v(-126.37, 2.57) * mm, v(-126.23, 3.92) * mm, v(-125.95, 5.8) * mm, v(-125.44, 8.25) * mm, v(-124.57, 11.4) * mm, v(-123.44, 14.7) * mm, v(-121.62, 19.33) * mm, v(-118.77, 25.43) * mm, v(-114.67, 33.14) * mm, v(-110.1, 41.14) * mm, v(-105.34, 49.38) * mm, v(-101.43, 56.47) * mm, v(-98.47, 62.31) * mm, v(-96.37, 66.81) * mm, v(-94.44, 71.44) * mm, v(-93, 75.45) * mm, v(-92, 78.76) * mm, v(-91.33, 81.3) * mm, v(-90.75, 83.9) * mm, v(-90.35, 86.12) * mm, v(-90.1, 87.93) * mm, v(-89.88, 89.73) * mm, v(-89.7, 91.94) * mm, v(-89.6, 94.53) * mm, v(-89.61, 97.06) * mm, v(-89.72, 99.51) * mm, v(-89.98, 102.68) * mm, v(-90.47, 106.44) * mm, v(-91.26, 110.63) * mm, v(-92.14, 114.5) * mm, v(-93.04, 118.06) * mm, v(-94.2, 122.4) * mm, v(-95.17, 126.15) * mm, v(-95.82, 129.29) * mm, v(-96.14, 131.32) * mm, v(-96.3, 133.04) * mm, v(-96.31, 134.46) * mm, v(-96.23, 135.45) * mm, v(-96.11, 136.18) * mm, v(-96.02, 136.62) * mm, v(-95.93, 136.97) * mm, v(-95.85, 137.24) * mm, v(-95.76, 137.52) * mm, v(-95.62, 137.93) * mm, v(-95.4, 138.5) * mm, v(-94.93, 139.51) * mm, v(-94.14, 140.98) * mm, v(-92.83, 143) * mm, v(-91.14, 145.21) * mm, v(-89.1, 147.56) * mm, v(-86.7, 150.02) * mm, v(-83.04, 153.37) * mm, v(-77.67, 157.62) * mm, v(-70.12, 162.62) * mm, v(-61.63, 167.33) * mm, v(-52.35, 171.62) * mm, v(-42.46, 175.35) * mm, v(-32.12, 178.4) * mm, v(-23.26, 180.32) * mm, v(-16.1, 181.41) * mm, v(-10.72, 182.01) * mm, v(-6.24, 182.32) * mm, v(-2.67, 182.44) * mm, v(0, 182.47) * mm, v(2.67, 182.44) * mm, v(6.24, 182.32) * mm, v(10.72, 182.01) * mm, v(16.1, 181.41) * mm, v(23.26, 180.32) * mm, v(32.12, 178.4) * mm, v(42.46, 175.35) * mm, v(52.35, 171.62) * mm, v(61.63, 167.33) * mm, v(70.12, 162.62) * mm, v(77.67, 157.62) * mm, v(83.04, 153.37) * mm, v(86.7, 150.02) * mm, v(89.1, 147.56) * mm, v(91.14, 145.21) * mm, v(92.83, 143) * mm, v(94.14, 140.98) * mm, v(94.93, 139.51) * mm, v(95.4, 138.5) * mm, v(95.62, 137.93) * mm, v(95.76, 137.52) * mm, v(95.85, 137.24) * mm, v(95.93, 136.97) * mm, v(96.02, 136.62) * mm, v(96.11, 136.18) * mm, v(96.23, 135.45) * mm, v(96.31, 134.46) * mm, v(96.3, 133.04) * mm, v(96.14, 131.32) * mm, v(95.82, 129.29) * mm, v(95.17, 126.15) * mm, v(94.2, 122.4) * mm, v(93.04, 118.06) * mm, v(92.14, 114.5) * mm, v(91.26, 110.63) * mm, v(90.47, 106.44) * mm, v(89.98, 102.68) * mm, v(89.72, 99.51) * mm, v(89.61, 97.06) * mm, v(89.6, 94.53) * mm, v(89.7, 91.94) * mm, v(89.88, 89.73) * mm, v(90.1, 87.93) * mm, v(90.35, 86.12) * mm, v(90.75, 83.9) * mm, v(91.33, 81.3) * mm, v(92, 78.76) * mm, v(93, 75.45) * mm, v(94.44, 71.44) * mm, v(96.37, 66.81) * mm, v(98.47, 62.31) * mm, v(101.43, 56.47) * mm, v(105.34, 49.38) * mm, v(110.1, 41.14) * mm, v(114.67, 33.14) * mm, v(118.77, 25.43) * mm, v(121.62, 19.33) * mm, v(123.44, 14.7) * mm, v(124.57, 11.4) * mm, v(125.44, 8.25) * mm, v(125.95, 5.8) * mm, v(126.23, 3.92) * mm, v(126.37, 2.57) * mm, v(126.45, 1.48) * mm, v(126.48, 0.62) * mm, v(126.48, 0) * mm, v(126.48, -0.62) * mm, v(126.45, -1.48) * mm, v(126.37, -2.57) * mm, v(126.23, -3.92) * mm, v(125.95, -5.8) * mm, v(125.44, -8.25) * mm, v(124.57, -11.4) * mm, v(123.44, -14.7) * mm, v(121.62, -19.33) * mm, v(118.77, -25.43) * mm, v(114.67, -33.14) * mm, v(110.1, -41.14) * mm, v(105.34, -49.38) * mm, v(101.43, -56.47) * mm, v(98.47, -62.31) * mm, v(96.37, -66.81) * mm, v(94.44, -71.44) * mm, v(93, -75.45) * mm, v(92, -78.76) * mm, v(91.33, -81.3) * mm, v(90.75, -83.9) * mm, v(90.35, -86.12) * mm, v(90.1, -87.93) * mm, v(89.88, -89.73) * mm, v(89.7, -91.94) * mm, v(89.6, -94.53) * mm, v(89.61, -97.06) * mm, v(89.72, -99.51) * mm, v(89.98, -102.68) * mm, v(90.47, -106.44) * mm, v(91.26, -110.63) * mm, v(92.14, -114.5) * mm, v(93.04, -118.06) * mm, v(94.2, -122.4) * mm, v(95.17, -126.15) * mm, v(95.82, -129.29) * mm, v(96.14, -131.32) * mm, v(96.3, -133.04) * mm, v(96.31, -134.46) * mm, v(96.23, -135.45) * mm, v(96.11, -136.18) * mm, v(96.02, -136.62) * mm, v(95.93, -136.97) * mm, v(95.85, -137.24) * mm, v(95.76, -137.52) * mm, v(95.62, -137.93) * mm, v(95.4, -138.5) * mm, v(94.93, -139.51) * mm, v(94.14, -140.98) * mm, v(92.83, -143) * mm, v(91.14, -145.21) * mm, v(89.1, -147.56) * mm, v(86.7, -150.02) * mm, v(83.04, -153.37) * mm, v(77.67, -157.62) * mm, v(70.12, -162.62) * mm, v(61.63, -167.33) * mm, v(52.35, -171.62) * mm, v(42.46, -175.35) * mm, v(32.12, -178.4) * mm, v(23.26, -180.32) * mm, v(16.1, -181.41) * mm, v(10.72, -182.01) * mm, v(6.24, -182.32) * mm, v(2.67, -182.44) * mm, v(0, -182.47) * mm, v(-2.67, -182.44) * mm, v(-6.24, -182.32) * mm, v(-10.72, -182.01) * mm, v(-16.1, -181.41) * mm, v(-23.26, -180.32) * mm, v(-32.12, -178.4) * mm, v(-42.46, -175.35) * mm, v(-52.35, -171.62) * mm, v(-61.63, -167.33) * mm, v(-70.12, -162.62) * mm, v(-77.67, -157.62) * mm, v(-83.04, -153.37) * mm, v(-86.7, -150.02) * mm, v(-89.1, -147.56) * mm, v(-91.14, -145.21) * mm, v(-92.83, -143) * mm, v(-94.14, -140.98) * mm, v(-94.93, -139.51) * mm, v(-95.4, -138.5) * mm, v(-95.62, -137.93) * mm, v(-95.76, -137.52) * mm, v(-95.85, -137.24) * mm, v(-95.93, -136.97) * mm, v(-96.02, -136.62) * mm, v(-96.11, -136.18) * mm, v(-96.23, -135.45) * mm, v(-96.31, -134.46) * mm, v(-96.3, -133.04) * mm, v(-96.14, -131.32) * mm, v(-95.82, -129.29) * mm, v(-95.17, -126.15) * mm, v(-94.2, -122.4) * mm, v(-93.04, -118.06) * mm, v(-92.14, -114.5) * mm, v(-91.26, -110.63) * mm, v(-90.47, -106.44) * mm, v(-89.98, -102.68) * mm, v(-89.72, -99.51) * mm, v(-89.61, -97.06) * mm, v(-89.6, -94.53) * mm, v(-89.7, -91.94) * mm, v(-89.88, -89.73) * mm, v(-90.1, -87.93) * mm, v(-90.35, -86.12) * mm, v(-90.75, -83.9) * mm, v(-91.33, -81.3) * mm, v(-92, -78.76) * mm, v(-93, -75.45) * mm, v(-94.44, -71.44) * mm, v(-96.37, -66.81) * mm, v(-98.47, -62.31) * mm, v(-101.43, -56.47) * mm, v(-105.34, -49.38) * mm, v(-110.1, -41.14) * mm, v(-114.67, -33.14) * mm, v(-118.77, -25.43) * mm, v(-121.62, -19.33) * mm, v(-123.44, -14.7) * mm, v(-124.57, -11.4) * mm, v(-125.44, -8.25) * mm, v(-125.95, -5.8) * mm, v(-126.23, -3.92) * mm, v(-126.37, -2.57) * mm, v(-126.45, -1.48) * mm, v(-126.48, -0.62) * mm, v(-126.48, 0) * mm, v(-126.48, 0.62) * mm]});
            skLineSegment(sketch, "E132", {"start": v(-77.84, 52.46) * mm, "end": v(-63.23, 78.19) * mm});
            skArc(sketch, "E133.trimOffspring", {"start": v(-63.23, 78.19) * mm, "mid": v(-68.37, 95.01) * mm, "end": v(-82.06, 106.06) * mm});
            skLineSegment(sketch, "E134.MirrorCS", {"start": v(-77.84, -52.46) * mm, "end": v(-63.23, -78.19) * mm});
            skLineSegment(sketch, "E135", {"start": v(0, 0) * mm, "end": v(0, 115.42) * mm, "construction": true});
            skLineSegment(sketch, "E136.MirrorCS", {"start": v(77.84, 52.46) * mm, "end": v(63.23, 78.19) * mm});
            skLineSegment(sketch, "E137.MirrorCS", {"start": v(77.84, -52.46) * mm, "end": v(63.23, -78.19) * mm});
            skArc(sketch, "E138.trimOffspring", {"start": v(63.23, 78.19) * mm, "mid": v(68.37, 95.01) * mm, "end": v(82.06, 106.06) * mm});
            skArc(sketch, "E139.trimOffspring", {"start": v(63.23, -78.19) * mm, "mid": v(68.37, -95.01) * mm, "end": v(82.06, -106.06) * mm});
            skArc(sketch, "E140.trimOffspring", {"start": v(-63.23, -78.19) * mm, "mid": v(-68.37, -95.01) * mm, "end": v(-82.06, -106.06) * mm});
            skArc(sketch, "E141", {"start": v(-90.8, -108.11) * mm, "mid": v(-91.7, -77.84) * mm, "end": v(-104.74, -50.51) * mm});
            skPoint(sketch, "E142.orphan", {"position": v(90.8, 108.11) * mm});
            skPoint(sketch, "E143.orphan", {"position": v(104.74, 50.51) * mm});
            skArc(sketch, "E144", {"start": v(-90.8, 108.11) * mm, "mid": v(-91.7, 77.84) * mm, "end": v(-104.74, 50.51) * mm});
            skArc(sketch, "E145", {"start": v(90.8, -108.11) * mm, "mid": v(91.7, -77.84) * mm, "end": v(104.74, -50.51) * mm});
            const initialGuessF2  = {"E92.0": [0, 0.08288104439999998, 1, 0, 0.13267715999999996, 0.11958350000000001, 0, 0.055173648266843435], "E93.MirrorC": [0, -0.08288104439999998, 1, 0, 0.13267715999999996, 0.11958350000000001, 3.141592653589793, 3.1966594490639286], "E109.trimOffspring": [0, -0.08288104439999998, 1, 0, 0.13267715999999996, 0.11958350000000001, 4.382070923725125, 5.042707037044202], "E110.trimOffspring": [0, 0.08288104439999998, 1, 0, 0.13267715999999996, 0.11958350000000001, 1.2404782701353567, 1.9011143834544768], "E111.trimOffspring": [0, 0.08288104439999998, 1, 0, 0.13267715999999996, 0.11958350000000001, 3.0865258581156554, 3.141592653589793], "E112.trimOffspring": [0, -0.08288104439999998, 1, 0, 0.13267715999999996, 0.11958350000000001, 6.228011658912739, 0], "E126.trimOffspring": [0, 0, 0, 1, 0.17, 0.105, 1.2777177637492358, 1.8638748898405504], "E127.trimOffspring": [0, 0, 0, 1, 0.17, 0.105, 5.386066886005411, 0.8971184211740499], "E128.trimOffspring": [0, 0, 0, 1, 0.17, 0.105, 4.419310417339036, 5.005467543430347], "E129.trimOffspring": [0, 0, 0, 1, 0.17, 0.105, 2.2444742324152895, 4.0387110747638495]};
            skSetInitialGuess(sketch, initialGuessF2);
            skSolve(sketch);
        }
        {
            var Q0;
            {var subQ0=sQuery(id+"F2.wireOp",EDGE,"E109.trimOffspring");var subQ1=sQuery(id+"F2.wireOp",EDGE,"E105");var subQ8=makeQuery(id+"F2.imprint","INTERSECT",VERTEX,{"disambiguationData":[OD(1.0)],"derivedFrom":[subQ1,subQ0]});Q0=makeQuery(id+"F2.imprint","IMPRINT",FACE,{"disambiguationData":[TD([[makeQuery(id+"F2.imprint","IMPRINT",EDGE,{"disambiguationData":[TD([[subQ8,-1.0]])],"derivedFrom":subQ1}),-1.0]])]});}
            var Q1;
            {var subQ0=sQuery(id+"F2.wireOp",EDGE,"E110.trimOffspring");var subQ1=sQuery(id+"F2.wireOp",EDGE,"E105");var subQ6=makeQuery(id+"F2.imprint","INTERSECT",VERTEX,{"derivedFrom":[subQ1,subQ0]});Q1=makeQuery(id+"F2.imprint","IMPRINT",FACE,{"disambiguationData":[TD([[makeQuery(id+"F2.imprint","IMPRINT",EDGE,{"disambiguationData":[TD([[subQ6,1.0]])],"derivedFrom":subQ1}),-1.0]])]});}
            extrude(context, id + "F3", {"entities" : qUnion([Q0, Q1]), "depth" : 20 * mm, "offsetDistance" : 25 * mm});
        }
        {
            var Q0;
            Q0=qCreatedBy(id+"F1.planeOp",FACE);
            var sketch = newSketch(context, id + "F4", { "sketchPlane" : qUnion([Q0])});
            skFitSpline(sketch, "E146.0.0", {"points": [v(-146.48, 0) * mm, v(-146.48, -31.99) * mm, v(-89.5, -87.65) * mm, v(-140.83, -150.23) * mm, v(0, -234.29) * mm, v(140.83, -150.23) * mm, v(89.5, -87.65) * mm, v(179.22, 0) * mm, v(89.5, 87.65) * mm, v(140.83, 150.23) * mm, v(0, 234.29) * mm, v(-140.83, 150.23) * mm, v(-89.5, 87.65) * mm, v(-146.48, 31.99) * mm, v(-146.48, 0) * mm]});
            skEllipticalArc(sketch, "E146.0.1", {});
            skFitSpline(sketch, "E146.0.2", {"points": [v(-146.48, 0) * mm, v(-146.48, -31.99) * mm, v(-89.5, -87.65) * mm, v(-140.83, -150.23) * mm, v(0, -234.29) * mm, v(140.83, -150.23) * mm, v(89.5, -87.65) * mm, v(179.22, 0) * mm, v(89.5, 87.65) * mm, v(140.83, 150.23) * mm, v(0, 234.29) * mm, v(-140.83, 150.23) * mm, v(-89.5, 87.65) * mm, v(-146.48, 31.99) * mm, v(-146.48, 0) * mm]});
            skEllipticalArc(sketch, "E146.0.3", {});
            skArc(sketch, "E147.0", {"start": v(-90.8, 108.11) * mm, "mid": v(-91.7, 77.84) * mm, "end": v(-104.74, 50.51) * mm});
            skFitSpline(sketch, "E148.0", {"points": [v(-126.48, 0) * mm, v(-126.48, 0.2) * mm, v(-126.48, 0.62) * mm, v(-126.45, 1.48) * mm, v(-126.37, 2.57) * mm, v(-126.23, 3.92) * mm, v(-125.95, 5.8) * mm, v(-125.44, 8.25) * mm, v(-124.57, 11.4) * mm, v(-123.44, 14.7) * mm, v(-121.62, 19.33) * mm, v(-118.77, 25.43) * mm, v(-114.67, 33.14) * mm, v(-110.1, 41.14) * mm, v(-105.34, 49.38) * mm, v(-101.43, 56.47) * mm, v(-98.47, 62.31) * mm, v(-96.37, 66.81) * mm, v(-94.44, 71.44) * mm, v(-93, 75.45) * mm, v(-92, 78.76) * mm, v(-91.33, 81.3) * mm, v(-90.75, 83.9) * mm, v(-90.35, 86.12) * mm, v(-90.1, 87.93) * mm, v(-89.88, 89.73) * mm, v(-89.7, 91.94) * mm, v(-89.6, 94.53) * mm, v(-89.61, 97.06) * mm, v(-89.72, 99.51) * mm, v(-89.98, 102.68) * mm, v(-90.47, 106.44) * mm, v(-91.26, 110.63) * mm, v(-92.14, 114.5) * mm, v(-93.04, 118.06) * mm, v(-94.2, 122.4) * mm, v(-95.17, 126.15) * mm, v(-95.82, 129.29) * mm, v(-96.14, 131.32) * mm, v(-96.3, 133.04) * mm, v(-96.31, 134.46) * mm, v(-96.23, 135.45) * mm, v(-96.11, 136.18) * mm, v(-96.02, 136.62) * mm, v(-95.93, 136.97) * mm, v(-95.85, 137.24) * mm, v(-95.76, 137.52) * mm, v(-95.62, 137.93) * mm, v(-95.4, 138.5) * mm, v(-94.93, 139.51) * mm, v(-94.14, 140.98) * mm, v(-92.83, 143) * mm, v(-91.14, 145.21) * mm, v(-89.1, 147.56) * mm, v(-86.7, 150.02) * mm, v(-83.04, 153.37) * mm, v(-77.67, 157.62) * mm, v(-70.12, 162.62) * mm, v(-61.63, 167.33) * mm, v(-52.35, 171.62) * mm, v(-42.46, 175.35) * mm, v(-32.12, 178.4) * mm, v(-23.26, 180.32) * mm, v(-16.1, 181.41) * mm, v(-10.72, 182.01) * mm, v(-6.24, 182.32) * mm, v(-2.67, 182.44) * mm, v(0, 182.47) * mm, v(2.67, 182.44) * mm, v(6.24, 182.32) * mm, v(10.72, 182.01) * mm, v(16.1, 181.41) * mm, v(23.26, 180.32) * mm, v(32.12, 178.4) * mm, v(42.46, 175.35) * mm, v(52.35, 171.62) * mm, v(61.63, 167.33) * mm, v(70.12, 162.62) * mm, v(77.67, 157.62) * mm, v(83.04, 153.37) * mm, v(86.7, 150.02) * mm, v(89.1, 147.56) * mm, v(91.14, 145.21) * mm, v(92.83, 143) * mm, v(94.14, 140.98) * mm, v(94.93, 139.51) * mm, v(95.4, 138.5) * mm, v(95.62, 137.93) * mm, v(95.76, 137.52) * mm, v(95.85, 137.24) * mm, v(95.93, 136.97) * mm, v(96.02, 136.62) * mm, v(96.11, 136.18) * mm, v(96.23, 135.45) * mm, v(96.31, 134.46) * mm, v(96.3, 133.04) * mm, v(96.14, 131.32) * mm, v(95.82, 129.29) * mm, v(95.17, 126.15) * mm, v(94.2, 122.4) * mm, v(93.04, 118.06) * mm, v(92.14, 114.5) * mm, v(91.26, 110.63) * mm, v(90.47, 106.44) * mm, v(89.98, 102.68) * mm, v(89.72, 99.51) * mm, v(89.61, 97.06) * mm, v(89.6, 94.53) * mm, v(89.7, 91.94) * mm, v(89.88, 89.73) * mm, v(90.1, 87.93) * mm, v(90.35, 86.12) * mm, v(90.75, 83.9) * mm, v(91.33, 81.3) * mm, v(92, 78.76) * mm, v(93, 75.45) * mm, v(94.44, 71.44) * mm, v(96.37, 66.81) * mm, v(98.47, 62.31) * mm, v(101.43, 56.47) * mm, v(105.34, 49.38) * mm, v(110.1, 41.14) * mm, v(114.67, 33.14) * mm, v(118.77, 25.43) * mm, v(121.62, 19.33) * mm, v(123.44, 14.7) * mm, v(124.57, 11.4) * mm, v(125.44, 8.25) * mm, v(125.95, 5.8) * mm, v(126.23, 3.92) * mm, v(126.37, 2.57) * mm, v(126.45, 1.48) * mm, v(126.48, 0.62) * mm, v(126.48, 0) * mm, v(126.48, -0.62) * mm, v(126.45, -1.48) * mm, v(126.37, -2.57) * mm, v(126.23, -3.92) * mm, v(125.95, -5.8) * mm, v(125.44, -8.25) * mm, v(124.57, -11.4) * mm, v(123.44, -14.7) * mm, v(121.62, -19.33) * mm, v(118.77, -25.43) * mm, v(114.67, -33.14) * mm, v(110.1, -41.14) * mm, v(105.34, -49.38) * mm, v(101.43, -56.47) * mm, v(98.47, -62.31) * mm, v(96.37, -66.81) * mm, v(94.44, -71.44) * mm, v(93, -75.45) * mm, v(92, -78.76) * mm, v(91.33, -81.3) * mm, v(90.75, -83.9) * mm, v(90.35, -86.12) * mm, v(90.1, -87.93) * mm, v(89.88, -89.73) * mm, v(89.7, -91.94) * mm, v(89.6, -94.53) * mm, v(89.61, -97.06) * mm, v(89.72, -99.51) * mm, v(89.98, -102.68) * mm, v(90.47, -106.44) * mm, v(91.26, -110.63) * mm, v(92.14, -114.5) * mm, v(93.04, -118.06) * mm, v(94.2, -122.4) * mm, v(95.17, -126.15) * mm, v(95.82, -129.29) * mm, v(96.14, -131.32) * mm, v(96.3, -133.04) * mm, v(96.31, -134.46) * mm, v(96.23, -135.45) * mm, v(96.11, -136.18) * mm, v(96.02, -136.62) * mm, v(95.93, -136.97) * mm, v(95.85, -137.24) * mm, v(95.76, -137.52) * mm, v(95.62, -137.93) * mm, v(95.4, -138.5) * mm, v(94.93, -139.51) * mm, v(94.14, -140.98) * mm, v(92.83, -143) * mm, v(91.14, -145.21) * mm, v(89.1, -147.56) * mm, v(86.7, -150.02) * mm, v(83.04, -153.37) * mm, v(77.67, -157.62) * mm, v(70.12, -162.62) * mm, v(61.63, -167.33) * mm, v(52.35, -171.62) * mm, v(42.46, -175.35) * mm, v(32.12, -178.4) * mm, v(23.26, -180.32) * mm, v(16.1, -181.41) * mm, v(10.72, -182.01) * mm, v(6.24, -182.32) * mm, v(2.67, -182.44) * mm, v(0, -182.47) * mm, v(-2.67, -182.44) * mm, v(-6.24, -182.32) * mm, v(-10.72, -182.01) * mm, v(-16.1, -181.41) * mm, v(-23.26, -180.32) * mm, v(-32.12, -178.4) * mm, v(-42.46, -175.35) * mm, v(-52.35, -171.62) * mm, v(-61.63, -167.33) * mm, v(-70.12, -162.62) * mm, v(-77.67, -157.62) * mm, v(-83.04, -153.37) * mm, v(-86.7, -150.02) * mm, v(-89.1, -147.56) * mm, v(-91.14, -145.21) * mm, v(-92.83, -143) * mm, v(-94.14, -140.98) * mm, v(-94.93, -139.51) * mm, v(-95.4, -138.5) * mm, v(-95.62, -137.93) * mm, v(-95.76, -137.52) * mm, v(-95.85, -137.24) * mm, v(-95.93, -136.97) * mm, v(-96.02, -136.62) * mm, v(-96.11, -136.18) * mm, v(-96.23, -135.45) * mm, v(-96.31, -134.46) * mm, v(-96.3, -133.04) * mm, v(-96.14, -131.32) * mm, v(-95.82, -129.29) * mm, v(-95.17, -126.15) * mm, v(-94.2, -122.4) * mm, v(-93.04, -118.06) * mm, v(-92.14, -114.5) * mm, v(-91.26, -110.63) * mm, v(-90.47, -106.44) * mm, v(-89.98, -102.68) * mm, v(-89.72, -99.51) * mm, v(-89.61, -97.06) * mm, v(-89.6, -94.53) * mm, v(-89.7, -91.94) * mm, v(-89.88, -89.73) * mm, v(-90.1, -87.93) * mm, v(-90.35, -86.12) * mm, v(-90.75, -83.9) * mm, v(-91.33, -81.3) * mm, v(-92, -78.76) * mm, v(-93, -75.45) * mm, v(-94.44, -71.44) * mm, v(-96.37, -66.81) * mm, v(-98.47, -62.31) * mm, v(-101.43, -56.47) * mm, v(-105.34, -49.38) * mm, v(-110.1, -41.14) * mm, v(-114.67, -33.14) * mm, v(-118.77, -25.43) * mm, v(-121.62, -19.33) * mm, v(-123.44, -14.7) * mm, v(-124.57, -11.4) * mm, v(-125.44, -8.25) * mm, v(-125.95, -5.8) * mm, v(-126.23, -3.92) * mm, v(-126.37, -2.57) * mm, v(-126.45, -1.48) * mm, v(-126.48, -0.62) * mm, v(-126.48, -0.2) * mm, v(-126.48, 0) * mm]});
            skArc(sketch, "E149.0", {"start": v(90.8, -108.11) * mm, "mid": v(91.7, -77.84) * mm, "end": v(104.74, -50.51) * mm});
            skFitSpline(sketch, "E150.0", {"points": [v(-126.48, 0) * mm, v(-126.48, 0.2) * mm, v(-126.48, 0.62) * mm, v(-126.45, 1.48) * mm, v(-126.37, 2.57) * mm, v(-126.23, 3.92) * mm, v(-125.95, 5.8) * mm, v(-125.44, 8.25) * mm, v(-124.57, 11.4) * mm, v(-123.44, 14.7) * mm, v(-121.62, 19.33) * mm, v(-118.77, 25.43) * mm, v(-114.67, 33.14) * mm, v(-110.1, 41.14) * mm, v(-105.34, 49.38) * mm, v(-101.43, 56.47) * mm, v(-98.47, 62.31) * mm, v(-96.37, 66.81) * mm, v(-94.44, 71.44) * mm, v(-93, 75.45) * mm, v(-92, 78.76) * mm, v(-91.33, 81.3) * mm, v(-90.75, 83.9) * mm, v(-90.35, 86.12) * mm, v(-90.1, 87.93) * mm, v(-89.88, 89.73) * mm, v(-89.7, 91.94) * mm, v(-89.6, 94.53) * mm, v(-89.61, 97.06) * mm, v(-89.72, 99.51) * mm, v(-89.98, 102.68) * mm, v(-90.47, 106.44) * mm, v(-91.26, 110.63) * mm, v(-92.14, 114.5) * mm, v(-93.04, 118.06) * mm, v(-94.2, 122.4) * mm, v(-95.17, 126.15) * mm, v(-95.82, 129.29) * mm, v(-96.14, 131.32) * mm, v(-96.3, 133.04) * mm, v(-96.31, 134.46) * mm, v(-96.23, 135.45) * mm, v(-96.11, 136.18) * mm, v(-96.02, 136.62) * mm, v(-95.93, 136.97) * mm, v(-95.85, 137.24) * mm, v(-95.76, 137.52) * mm, v(-95.62, 137.93) * mm, v(-95.4, 138.5) * mm, v(-94.93, 139.51) * mm, v(-94.14, 140.98) * mm, v(-92.83, 143) * mm, v(-91.14, 145.21) * mm, v(-89.1, 147.56) * mm, v(-86.7, 150.02) * mm, v(-83.04, 153.37) * mm, v(-77.67, 157.62) * mm, v(-70.12, 162.62) * mm, v(-61.63, 167.33) * mm, v(-52.35, 171.62) * mm, v(-42.46, 175.35) * mm, v(-32.12, 178.4) * mm, v(-23.26, 180.32) * mm, v(-16.1, 181.41) * mm, v(-10.72, 182.01) * mm, v(-6.24, 182.32) * mm, v(-2.67, 182.44) * mm, v(0, 182.47) * mm, v(2.67, 182.44) * mm, v(6.24, 182.32) * mm, v(10.72, 182.01) * mm, v(16.1, 181.41) * mm, v(23.26, 180.32) * mm, v(32.12, 178.4) * mm, v(42.46, 175.35) * mm, v(52.35, 171.62) * mm, v(61.63, 167.33) * mm, v(70.12, 162.62) * mm, v(77.67, 157.62) * mm, v(83.04, 153.37) * mm, v(86.7, 150.02) * mm, v(89.1, 147.56) * mm, v(91.14, 145.21) * mm, v(92.83, 143) * mm, v(94.14, 140.98) * mm, v(94.93, 139.51) * mm, v(95.4, 138.5) * mm, v(95.62, 137.93) * mm, v(95.76, 137.52) * mm, v(95.85, 137.24) * mm, v(95.93, 136.97) * mm, v(96.02, 136.62) * mm, v(96.11, 136.18) * mm, v(96.23, 135.45) * mm, v(96.31, 134.46) * mm, v(96.3, 133.04) * mm, v(96.14, 131.32) * mm, v(95.82, 129.29) * mm, v(95.17, 126.15) * mm, v(94.2, 122.4) * mm, v(93.04, 118.06) * mm, v(92.14, 114.5) * mm, v(91.26, 110.63) * mm, v(90.47, 106.44) * mm, v(89.98, 102.68) * mm, v(89.72, 99.51) * mm, v(89.61, 97.06) * mm, v(89.6, 94.53) * mm, v(89.7, 91.94) * mm, v(89.88, 89.73) * mm, v(90.1, 87.93) * mm, v(90.35, 86.12) * mm, v(90.75, 83.9) * mm, v(91.33, 81.3) * mm, v(92, 78.76) * mm, v(93, 75.45) * mm, v(94.44, 71.44) * mm, v(96.37, 66.81) * mm, v(98.47, 62.31) * mm, v(101.43, 56.47) * mm, v(105.34, 49.38) * mm, v(110.1, 41.14) * mm, v(114.67, 33.14) * mm, v(118.77, 25.43) * mm, v(121.62, 19.33) * mm, v(123.44, 14.7) * mm, v(124.57, 11.4) * mm, v(125.44, 8.25) * mm, v(125.95, 5.8) * mm, v(126.23, 3.92) * mm, v(126.37, 2.57) * mm, v(126.45, 1.48) * mm, v(126.48, 0.62) * mm, v(126.48, 0) * mm, v(126.48, -0.62) * mm, v(126.45, -1.48) * mm, v(126.37, -2.57) * mm, v(126.23, -3.92) * mm, v(125.95, -5.8) * mm, v(125.44, -8.25) * mm, v(124.57, -11.4) * mm, v(123.44, -14.7) * mm, v(121.62, -19.33) * mm, v(118.77, -25.43) * mm, v(114.67, -33.14) * mm, v(110.1, -41.14) * mm, v(105.34, -49.38) * mm, v(101.43, -56.47) * mm, v(98.47, -62.31) * mm, v(96.37, -66.81) * mm, v(94.44, -71.44) * mm, v(93, -75.45) * mm, v(92, -78.76) * mm, v(91.33, -81.3) * mm, v(90.75, -83.9) * mm, v(90.35, -86.12) * mm, v(90.1, -87.93) * mm, v(89.88, -89.73) * mm, v(89.7, -91.94) * mm, v(89.6, -94.53) * mm, v(89.61, -97.06) * mm, v(89.72, -99.51) * mm, v(89.98, -102.68) * mm, v(90.47, -106.44) * mm, v(91.26, -110.63) * mm, v(92.14, -114.5) * mm, v(93.04, -118.06) * mm, v(94.2, -122.4) * mm, v(95.17, -126.15) * mm, v(95.82, -129.29) * mm, v(96.14, -131.32) * mm, v(96.3, -133.04) * mm, v(96.31, -134.46) * mm, v(96.23, -135.45) * mm, v(96.11, -136.18) * mm, v(96.02, -136.62) * mm, v(95.93, -136.97) * mm, v(95.85, -137.24) * mm, v(95.76, -137.52) * mm, v(95.62, -137.93) * mm, v(95.4, -138.5) * mm, v(94.93, -139.51) * mm, v(94.14, -140.98) * mm, v(92.83, -143) * mm, v(91.14, -145.21) * mm, v(89.1, -147.56) * mm, v(86.7, -150.02) * mm, v(83.04, -153.37) * mm, v(77.67, -157.62) * mm, v(70.12, -162.62) * mm, v(61.63, -167.33) * mm, v(52.35, -171.62) * mm, v(42.46, -175.35) * mm, v(32.12, -178.4) * mm, v(23.26, -180.32) * mm, v(16.1, -181.41) * mm, v(10.72, -182.01) * mm, v(6.24, -182.32) * mm, v(2.67, -182.44) * mm, v(0, -182.47) * mm, v(-2.67, -182.44) * mm, v(-6.24, -182.32) * mm, v(-10.72, -182.01) * mm, v(-16.1, -181.41) * mm, v(-23.26, -180.32) * mm, v(-32.12, -178.4) * mm, v(-42.46, -175.35) * mm, v(-52.35, -171.62) * mm, v(-61.63, -167.33) * mm, v(-70.12, -162.62) * mm, v(-77.67, -157.62) * mm, v(-83.04, -153.37) * mm, v(-86.7, -150.02) * mm, v(-89.1, -147.56) * mm, v(-91.14, -145.21) * mm, v(-92.83, -143) * mm, v(-94.14, -140.98) * mm, v(-94.93, -139.51) * mm, v(-95.4, -138.5) * mm, v(-95.62, -137.93) * mm, v(-95.76, -137.52) * mm, v(-95.85, -137.24) * mm, v(-95.93, -136.97) * mm, v(-96.02, -136.62) * mm, v(-96.11, -136.18) * mm, v(-96.23, -135.45) * mm, v(-96.31, -134.46) * mm, v(-96.3, -133.04) * mm, v(-96.14, -131.32) * mm, v(-95.82, -129.29) * mm, v(-95.17, -126.15) * mm, v(-94.2, -122.4) * mm, v(-93.04, -118.06) * mm, v(-92.14, -114.5) * mm, v(-91.26, -110.63) * mm, v(-90.47, -106.44) * mm, v(-89.98, -102.68) * mm, v(-89.72, -99.51) * mm, v(-89.61, -97.06) * mm, v(-89.6, -94.53) * mm, v(-89.7, -91.94) * mm, v(-89.88, -89.73) * mm, v(-90.1, -87.93) * mm, v(-90.35, -86.12) * mm, v(-90.75, -83.9) * mm, v(-91.33, -81.3) * mm, v(-92, -78.76) * mm, v(-93, -75.45) * mm, v(-94.44, -71.44) * mm, v(-96.37, -66.81) * mm, v(-98.47, -62.31) * mm, v(-101.43, -56.47) * mm, v(-105.34, -49.38) * mm, v(-110.1, -41.14) * mm, v(-114.67, -33.14) * mm, v(-118.77, -25.43) * mm, v(-121.62, -19.33) * mm, v(-123.44, -14.7) * mm, v(-124.57, -11.4) * mm, v(-125.44, -8.25) * mm, v(-125.95, -5.8) * mm, v(-126.23, -3.92) * mm, v(-126.37, -2.57) * mm, v(-126.45, -1.48) * mm, v(-126.48, -0.62) * mm, v(-126.48, -0.2) * mm, v(-126.48, 0) * mm]});
            skArc(sketch, "E151.0", {"start": v(-90.8, -108.11) * mm, "mid": v(-91.7, -77.84) * mm, "end": v(-104.74, -50.51) * mm});
            skFitSpline(sketch, "E152.0", {"points": [v(-126.48, 0) * mm, v(-126.48, 0.2) * mm, v(-126.48, 0.62) * mm, v(-126.45, 1.48) * mm, v(-126.37, 2.57) * mm, v(-126.23, 3.92) * mm, v(-125.95, 5.8) * mm, v(-125.44, 8.25) * mm, v(-124.57, 11.4) * mm, v(-123.44, 14.7) * mm, v(-121.62, 19.33) * mm, v(-118.77, 25.43) * mm, v(-114.67, 33.14) * mm, v(-110.1, 41.14) * mm, v(-105.34, 49.38) * mm, v(-101.43, 56.47) * mm, v(-98.47, 62.31) * mm, v(-96.37, 66.81) * mm, v(-94.44, 71.44) * mm, v(-93, 75.45) * mm, v(-92, 78.76) * mm, v(-91.33, 81.3) * mm, v(-90.75, 83.9) * mm, v(-90.35, 86.12) * mm, v(-90.1, 87.93) * mm, v(-89.88, 89.73) * mm, v(-89.7, 91.94) * mm, v(-89.6, 94.53) * mm, v(-89.61, 97.06) * mm, v(-89.72, 99.51) * mm, v(-89.98, 102.68) * mm, v(-90.47, 106.44) * mm, v(-91.26, 110.63) * mm, v(-92.14, 114.5) * mm, v(-93.04, 118.06) * mm, v(-94.2, 122.4) * mm, v(-95.17, 126.15) * mm, v(-95.82, 129.29) * mm, v(-96.14, 131.32) * mm, v(-96.3, 133.04) * mm, v(-96.31, 134.46) * mm, v(-96.23, 135.45) * mm, v(-96.11, 136.18) * mm, v(-96.02, 136.62) * mm, v(-95.93, 136.97) * mm, v(-95.85, 137.24) * mm, v(-95.76, 137.52) * mm, v(-95.62, 137.93) * mm, v(-95.4, 138.5) * mm, v(-94.93, 139.51) * mm, v(-94.14, 140.98) * mm, v(-92.83, 143) * mm, v(-91.14, 145.21) * mm, v(-89.1, 147.56) * mm, v(-86.7, 150.02) * mm, v(-83.04, 153.37) * mm, v(-77.67, 157.62) * mm, v(-70.12, 162.62) * mm, v(-61.63, 167.33) * mm, v(-52.35, 171.62) * mm, v(-42.46, 175.35) * mm, v(-32.12, 178.4) * mm, v(-23.26, 180.32) * mm, v(-16.1, 181.41) * mm, v(-10.72, 182.01) * mm, v(-6.24, 182.32) * mm, v(-2.67, 182.44) * mm, v(0, 182.47) * mm, v(2.67, 182.44) * mm, v(6.24, 182.32) * mm, v(10.72, 182.01) * mm, v(16.1, 181.41) * mm, v(23.26, 180.32) * mm, v(32.12, 178.4) * mm, v(42.46, 175.35) * mm, v(52.35, 171.62) * mm, v(61.63, 167.33) * mm, v(70.12, 162.62) * mm, v(77.67, 157.62) * mm, v(83.04, 153.37) * mm, v(86.7, 150.02) * mm, v(89.1, 147.56) * mm, v(91.14, 145.21) * mm, v(92.83, 143) * mm, v(94.14, 140.98) * mm, v(94.93, 139.51) * mm, v(95.4, 138.5) * mm, v(95.62, 137.93) * mm, v(95.76, 137.52) * mm, v(95.85, 137.24) * mm, v(95.93, 136.97) * mm, v(96.02, 136.62) * mm, v(96.11, 136.18) * mm, v(96.23, 135.45) * mm, v(96.31, 134.46) * mm, v(96.3, 133.04) * mm, v(96.14, 131.32) * mm, v(95.82, 129.29) * mm, v(95.17, 126.15) * mm, v(94.2, 122.4) * mm, v(93.04, 118.06) * mm, v(92.14, 114.5) * mm, v(91.26, 110.63) * mm, v(90.47, 106.44) * mm, v(89.98, 102.68) * mm, v(89.72, 99.51) * mm, v(89.61, 97.06) * mm, v(89.6, 94.53) * mm, v(89.7, 91.94) * mm, v(89.88, 89.73) * mm, v(90.1, 87.93) * mm, v(90.35, 86.12) * mm, v(90.75, 83.9) * mm, v(91.33, 81.3) * mm, v(92, 78.76) * mm, v(93, 75.45) * mm, v(94.44, 71.44) * mm, v(96.37, 66.81) * mm, v(98.47, 62.31) * mm, v(101.43, 56.47) * mm, v(105.34, 49.38) * mm, v(110.1, 41.14) * mm, v(114.67, 33.14) * mm, v(118.77, 25.43) * mm, v(121.62, 19.33) * mm, v(123.44, 14.7) * mm, v(124.57, 11.4) * mm, v(125.44, 8.25) * mm, v(125.95, 5.8) * mm, v(126.23, 3.92) * mm, v(126.37, 2.57) * mm, v(126.45, 1.48) * mm, v(126.48, 0.62) * mm, v(126.48, 0) * mm, v(126.48, -0.62) * mm, v(126.45, -1.48) * mm, v(126.37, -2.57) * mm, v(126.23, -3.92) * mm, v(125.95, -5.8) * mm, v(125.44, -8.25) * mm, v(124.57, -11.4) * mm, v(123.44, -14.7) * mm, v(121.62, -19.33) * mm, v(118.77, -25.43) * mm, v(114.67, -33.14) * mm, v(110.1, -41.14) * mm, v(105.34, -49.38) * mm, v(101.43, -56.47) * mm, v(98.47, -62.31) * mm, v(96.37, -66.81) * mm, v(94.44, -71.44) * mm, v(93, -75.45) * mm, v(92, -78.76) * mm, v(91.33, -81.3) * mm, v(90.75, -83.9) * mm, v(90.35, -86.12) * mm, v(90.1, -87.93) * mm, v(89.88, -89.73) * mm, v(89.7, -91.94) * mm, v(89.6, -94.53) * mm, v(89.61, -97.06) * mm, v(89.72, -99.51) * mm, v(89.98, -102.68) * mm, v(90.47, -106.44) * mm, v(91.26, -110.63) * mm, v(92.14, -114.5) * mm, v(93.04, -118.06) * mm, v(94.2, -122.4) * mm, v(95.17, -126.15) * mm, v(95.82, -129.29) * mm, v(96.14, -131.32) * mm, v(96.3, -133.04) * mm, v(96.31, -134.46) * mm, v(96.23, -135.45) * mm, v(96.11, -136.18) * mm, v(96.02, -136.62) * mm, v(95.93, -136.97) * mm, v(95.85, -137.24) * mm, v(95.76, -137.52) * mm, v(95.62, -137.93) * mm, v(95.4, -138.5) * mm, v(94.93, -139.51) * mm, v(94.14, -140.98) * mm, v(92.83, -143) * mm, v(91.14, -145.21) * mm, v(89.1, -147.56) * mm, v(86.7, -150.02) * mm, v(83.04, -153.37) * mm, v(77.67, -157.62) * mm, v(70.12, -162.62) * mm, v(61.63, -167.33) * mm, v(52.35, -171.62) * mm, v(42.46, -175.35) * mm, v(32.12, -178.4) * mm, v(23.26, -180.32) * mm, v(16.1, -181.41) * mm, v(10.72, -182.01) * mm, v(6.24, -182.32) * mm, v(2.67, -182.44) * mm, v(0, -182.47) * mm, v(-2.67, -182.44) * mm, v(-6.24, -182.32) * mm, v(-10.72, -182.01) * mm, v(-16.1, -181.41) * mm, v(-23.26, -180.32) * mm, v(-32.12, -178.4) * mm, v(-42.46, -175.35) * mm, v(-52.35, -171.62) * mm, v(-61.63, -167.33) * mm, v(-70.12, -162.62) * mm, v(-77.67, -157.62) * mm, v(-83.04, -153.37) * mm, v(-86.7, -150.02) * mm, v(-89.1, -147.56) * mm, v(-91.14, -145.21) * mm, v(-92.83, -143) * mm, v(-94.14, -140.98) * mm, v(-94.93, -139.51) * mm, v(-95.4, -138.5) * mm, v(-95.62, -137.93) * mm, v(-95.76, -137.52) * mm, v(-95.85, -137.24) * mm, v(-95.93, -136.97) * mm, v(-96.02, -136.62) * mm, v(-96.11, -136.18) * mm, v(-96.23, -135.45) * mm, v(-96.31, -134.46) * mm, v(-96.3, -133.04) * mm, v(-96.14, -131.32) * mm, v(-95.82, -129.29) * mm, v(-95.17, -126.15) * mm, v(-94.2, -122.4) * mm, v(-93.04, -118.06) * mm, v(-92.14, -114.5) * mm, v(-91.26, -110.63) * mm, v(-90.47, -106.44) * mm, v(-89.98, -102.68) * mm, v(-89.72, -99.51) * mm, v(-89.61, -97.06) * mm, v(-89.6, -94.53) * mm, v(-89.7, -91.94) * mm, v(-89.88, -89.73) * mm, v(-90.1, -87.93) * mm, v(-90.35, -86.12) * mm, v(-90.75, -83.9) * mm, v(-91.33, -81.3) * mm, v(-92, -78.76) * mm, v(-93, -75.45) * mm, v(-94.44, -71.44) * mm, v(-96.37, -66.81) * mm, v(-98.47, -62.31) * mm, v(-101.43, -56.47) * mm, v(-105.34, -49.38) * mm, v(-110.1, -41.14) * mm, v(-114.67, -33.14) * mm, v(-118.77, -25.43) * mm, v(-121.62, -19.33) * mm, v(-123.44, -14.7) * mm, v(-124.57, -11.4) * mm, v(-125.44, -8.25) * mm, v(-125.95, -5.8) * mm, v(-126.23, -3.92) * mm, v(-126.37, -2.57) * mm, v(-126.45, -1.48) * mm, v(-126.48, -0.62) * mm, v(-126.48, -0.2) * mm, v(-126.48, 0) * mm]});
            skCircle(sketch, "E153.0", {"center": v(0, -192.5) * mm, "radius": 6 * mm});
            skCircle(sketch, "E154.0", {"center": v(0, 192.5) * mm, "radius": 6 * mm});
            skCircle(sketch, "E155", {"center": v(-102.5, 75) * mm, "radius": 5 * mm});
            skCircle(sketch, "E156.MirrorC", {"center": v(102.5, 75) * mm, "radius": 5 * mm});
            skCircle(sketch, "E157.MirrorC", {"center": v(102.5, -75) * mm, "radius": 5 * mm});
            skCircle(sketch, "E158.MirrorC", {"center": v(-102.5, -75) * mm, "radius": 5 * mm});
            const initialGuessF4  = {"E146.0.1": [0, 0.08288104439999998, 1, 0, 0.13267715999999996, 0.11958350000000001, 0.5183294966334667, 1.2404782701353567], "E146.0.3": [0, 0.08288104439999998, 1, 0, 0.13267715999999996, 0.11958350000000001, 1.90111438345274, 2.623263156960301]};
            skSetInitialGuess(sketch, initialGuessF4);
            skSolve(sketch);
        }
        {
            var Q0;
            Q0=makeQuery(id+"F4.imprint","IMPRINT",FACE,{"disambiguationData":[TD([[makeQuery(id+"F4.imprint","IMPRINT",EDGE,{"derivedFrom":sQuery(id+"F4.wireOp",EDGE,"E146.0.0")}),1.0]])]});
            extrude(context, id + "F5", {"entities" : qUnion([Q0]), "depth" : 20 * mm, "offsetDistance" : 25 * mm});
        }
        {
            var Q0;
            Q0=makeQuery(id+"F5.opExtrude","CAP_FACE",FACE,{"disambiguationData":[OSD([sQuery(id+"F4.wireOp",EDGE,"E146.0.0"),sQuery(id+"F4.wireOp",EDGE,"E146.0.1"),sQuery(id+"F4.wireOp",EDGE,"E146.0.2"),sQuery(id+"F4.wireOp",EDGE,"E146.0.3"),sQuery(id+"F4.wireOp",EDGE,"E147.0"),sQuery(id+"F4.wireOp",EDGE,"E148.0"),sQuery(id+"F4.wireOp",EDGE,"E149.0"),sQuery(id+"F4.wireOp",EDGE,"E150.0"),sQuery(id+"F4.wireOp",EDGE,"E151.0"),sQuery(id+"F4.wireOp",EDGE,"E152.0"),sQuery(id+"F4.wireOp",EDGE,"E153.0"),sQuery(id+"F4.wireOp",EDGE,"E154.0"),sQuery(id+"F4.wireOp",EDGE,"E155"),sQuery(id+"F4.wireOp",EDGE,"E156.MirrorC"),sQuery(id+"F4.wireOp",EDGE,"E157.MirrorC"),sQuery(id+"F4.wireOp",EDGE,"E158.MirrorC")])],"isStart":false});
            cPlane(context, id + "F6", {"entities" : qUnion([Q0]), "cplaneType" : CPlaneType.OFFSET, "offset" : 50 * mm, "width" : 150 * mm, "height" : 150 * mm});
        }
    });
